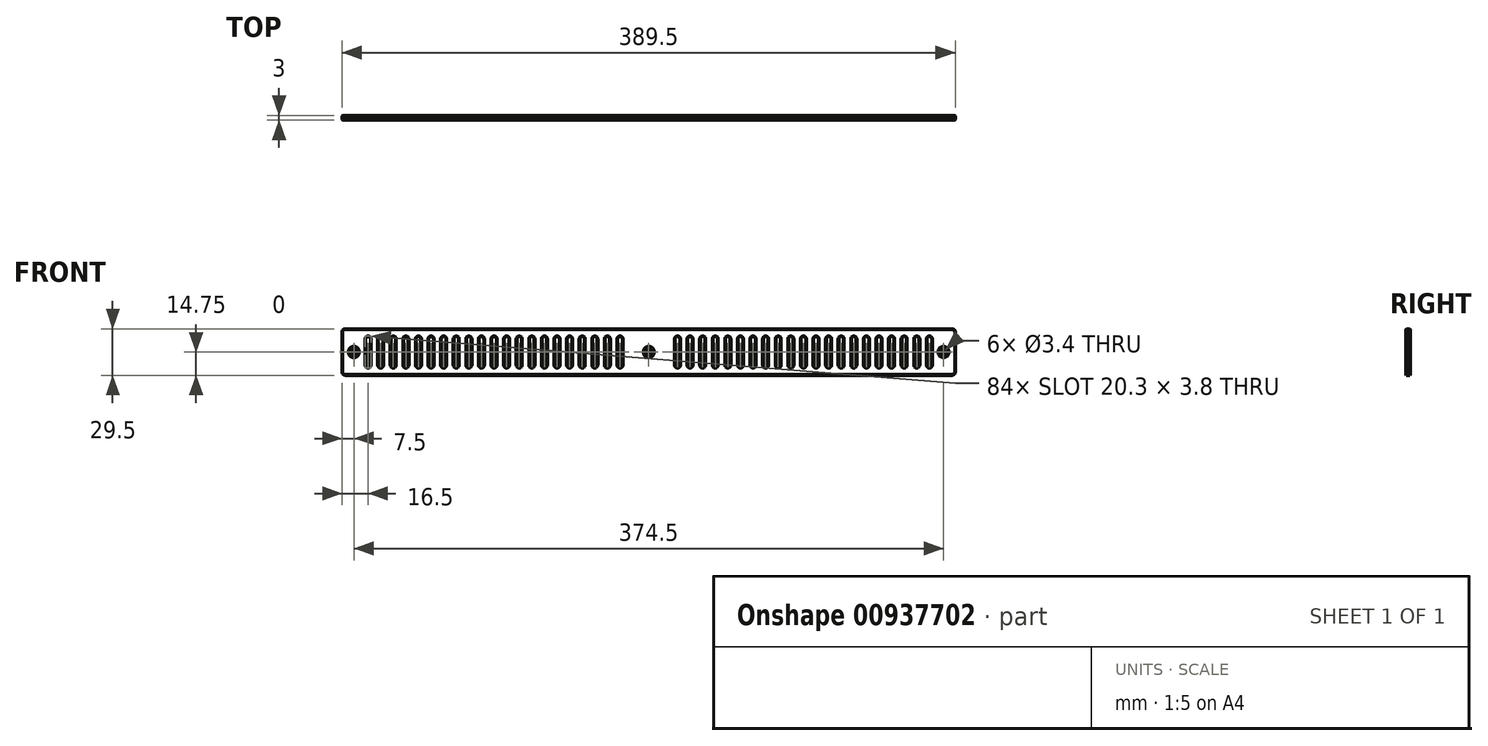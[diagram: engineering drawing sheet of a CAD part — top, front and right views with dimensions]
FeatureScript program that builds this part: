
annotation { "Feature Type Name" : "Feature", "Feature Type Description" : "" }
export const myFeature = defineFeature(function(context is Context, id is Id, definition is map)
    precondition{}
    {
        {
            var Q0;
            Q0=qCreatedBy(makeId("Front.planeOp"),FACE);
            var sketch = newSketch(context, id + "F0", { "sketchPlane" : qUnion([Q0])});
            skLineSegment(sketch, "E0.bottom", {"start": v(-194.75, 14.75) * mm, "end": v(194.75, 14.75) * mm});
            skLineSegment(sketch, "E0.top", {"start": v(-194.75, -14.75) * mm, "end": v(194.75, -14.75) * mm});
            skLineSegment(sketch, "E0.left", {"start": v(-194.75, 14.75) * mm, "end": v(-194.75, -14.75) * mm});
            skLineSegment(sketch, "E0.right", {"start": v(194.75, 14.75) * mm, "end": v(194.75, -14.75) * mm});
            skLineSegment(sketch, "E1.bottom", {"start": v(-178.25, 9.75) * mm, "end": v(-178.25, 9.75) * mm});
            skLineSegment(sketch, "E1.top", {"start": v(-178.25, -9.75) * mm, "end": v(-178.25, -9.75) * mm});
            skLineSegment(sketch, "E1.left", {"start": v(-179.75, 8.25) * mm, "end": v(-179.75, -8.25) * mm});
            skLineSegment(sketch, "E1.right", {"start": v(-176.75, 8.25) * mm, "end": v(-176.75, -8.25) * mm});
            skPoint(sketch, "E2.visualSharp", {"position": v(-179.75, 9.75) * mm});
            skArc(sketch, "E2.filletArc", {"start": v(-178.25, 9.75) * mm, "mid": v(-179.31, 9.31) * mm, "end": v(-179.75, 8.25) * mm});
            skPoint(sketch, "E3.visualSharp", {"position": v(-176.75, 9.75) * mm});
            skArc(sketch, "E3.filletArc", {"start": v(-176.75, 8.25) * mm, "mid": v(-177.19, 9.31) * mm, "end": v(-178.25, 9.75) * mm});
            skPoint(sketch, "E4.visualSharp", {"position": v(-179.75, -9.75) * mm});
            skArc(sketch, "E4.filletArc", {"start": v(-179.75, -8.25) * mm, "mid": v(-179.31, -9.31) * mm, "end": v(-178.25, -9.75) * mm});
            skPoint(sketch, "E5.visualSharp", {"position": v(-176.75, -9.75) * mm});
            skArc(sketch, "E5.filletArc", {"start": v(-178.25, -9.75) * mm, "mid": v(-177.19, -9.31) * mm, "end": v(-176.75, -8.25) * mm});
            skLineSegment(sketch, "E6.1.0.0", {"start": v(-171.75, 8.25) * mm, "end": v(-171.75, -8.25) * mm});
            skPoint(sketch, "E6.1.0.1", {"position": v(-168.75, -9.75) * mm});
            skPoint(sketch, "E6.1.0.2", {"position": v(-171.75, 9.75) * mm});
            skPoint(sketch, "E6.1.0.3", {"position": v(-171.75, -9.75) * mm});
            skLineSegment(sketch, "E6.1.0.4", {"start": v(-168.75, 8.25) * mm, "end": v(-168.75, -8.25) * mm});
            skPoint(sketch, "E6.1.0.5", {"position": v(-168.75, 9.75) * mm});
            skArc(sketch, "E6.1.0.6", {"start": v(-170.25, -9.75) * mm, "mid": v(-169.19, -9.31) * mm, "end": v(-168.75, -8.25) * mm});
            skArc(sketch, "E6.1.0.7", {"start": v(-170.25, 9.75) * mm, "mid": v(-171.31, 9.31) * mm, "end": v(-171.75, 8.25) * mm});
            skArc(sketch, "E6.1.0.8", {"start": v(-168.75, 8.25) * mm, "mid": v(-169.19, 9.31) * mm, "end": v(-170.25, 9.75) * mm});
            skArc(sketch, "E6.1.0.9", {"start": v(-171.75, -8.25) * mm, "mid": v(-171.31, -9.31) * mm, "end": v(-170.25, -9.75) * mm});
            skLineSegment(sketch, "E6.2.0.0", {"start": v(-163.75, 8.25) * mm, "end": v(-163.75, -8.25) * mm});
            skPoint(sketch, "E6.2.0.1", {"position": v(-160.75, -9.75) * mm});
            skPoint(sketch, "E6.2.0.2", {"position": v(-163.75, 9.75) * mm});
            skPoint(sketch, "E6.2.0.3", {"position": v(-163.75, -9.75) * mm});
            skLineSegment(sketch, "E6.2.0.4", {"start": v(-160.75, 8.25) * mm, "end": v(-160.75, -8.25) * mm});
            skPoint(sketch, "E6.2.0.5", {"position": v(-160.75, 9.75) * mm});
            skArc(sketch, "E6.2.0.6", {"start": v(-162.25, -9.75) * mm, "mid": v(-161.19, -9.31) * mm, "end": v(-160.75, -8.25) * mm});
            skArc(sketch, "E6.2.0.7", {"start": v(-162.25, 9.75) * mm, "mid": v(-163.31, 9.31) * mm, "end": v(-163.75, 8.25) * mm});
            skArc(sketch, "E6.2.0.8", {"start": v(-160.75, 8.25) * mm, "mid": v(-161.19, 9.31) * mm, "end": v(-162.25, 9.75) * mm});
            skArc(sketch, "E6.2.0.9", {"start": v(-163.75, -8.25) * mm, "mid": v(-163.31, -9.31) * mm, "end": v(-162.25, -9.75) * mm});
            skLineSegment(sketch, "E6.3.0.0", {"start": v(-155.75, 8.25) * mm, "end": v(-155.75, -8.25) * mm});
            skPoint(sketch, "E6.3.0.1", {"position": v(-152.75, -9.75) * mm});
            skPoint(sketch, "E6.3.0.2", {"position": v(-155.75, 9.75) * mm});
            skPoint(sketch, "E6.3.0.3", {"position": v(-155.75, -9.75) * mm});
            skLineSegment(sketch, "E6.3.0.4", {"start": v(-152.75, 8.25) * mm, "end": v(-152.75, -8.25) * mm});
            skPoint(sketch, "E6.3.0.5", {"position": v(-152.75, 9.75) * mm});
            skArc(sketch, "E6.3.0.6", {"start": v(-154.25, -9.75) * mm, "mid": v(-153.19, -9.31) * mm, "end": v(-152.75, -8.25) * mm});
            skArc(sketch, "E6.3.0.7", {"start": v(-154.25, 9.75) * mm, "mid": v(-155.31, 9.31) * mm, "end": v(-155.75, 8.25) * mm});
            skArc(sketch, "E6.3.0.8", {"start": v(-152.75, 8.25) * mm, "mid": v(-153.19, 9.31) * mm, "end": v(-154.25, 9.75) * mm});
            skArc(sketch, "E6.3.0.9", {"start": v(-155.75, -8.25) * mm, "mid": v(-155.31, -9.31) * mm, "end": v(-154.25, -9.75) * mm});
            skLineSegment(sketch, "E6.4.0.0", {"start": v(-147.75, 8.25) * mm, "end": v(-147.75, -8.25) * mm});
            skPoint(sketch, "E6.4.0.1", {"position": v(-144.75, -9.75) * mm});
            skPoint(sketch, "E6.4.0.2", {"position": v(-147.75, 9.75) * mm});
            skPoint(sketch, "E6.4.0.3", {"position": v(-147.75, -9.75) * mm});
            skLineSegment(sketch, "E6.4.0.4", {"start": v(-144.75, 8.25) * mm, "end": v(-144.75, -8.25) * mm});
            skPoint(sketch, "E6.4.0.5", {"position": v(-144.75, 9.75) * mm});
            skArc(sketch, "E6.4.0.6", {"start": v(-146.25, -9.75) * mm, "mid": v(-145.19, -9.31) * mm, "end": v(-144.75, -8.25) * mm});
            skArc(sketch, "E6.4.0.7", {"start": v(-146.25, 9.75) * mm, "mid": v(-147.31, 9.31) * mm, "end": v(-147.75, 8.25) * mm});
            skArc(sketch, "E6.4.0.8", {"start": v(-144.75, 8.25) * mm, "mid": v(-145.19, 9.31) * mm, "end": v(-146.25, 9.75) * mm});
            skArc(sketch, "E6.4.0.9", {"start": v(-147.75, -8.25) * mm, "mid": v(-147.31, -9.31) * mm, "end": v(-146.25, -9.75) * mm});
            skLineSegment(sketch, "E6.5.0.0", {"start": v(-139.75, 8.25) * mm, "end": v(-139.75, -8.25) * mm});
            skPoint(sketch, "E6.5.0.1", {"position": v(-136.75, -9.75) * mm});
            skPoint(sketch, "E6.5.0.2", {"position": v(-139.75, 9.75) * mm});
            skPoint(sketch, "E6.5.0.3", {"position": v(-139.75, -9.75) * mm});
            skLineSegment(sketch, "E6.5.0.4", {"start": v(-136.75, 8.25) * mm, "end": v(-136.75, -8.25) * mm});
            skPoint(sketch, "E6.5.0.5", {"position": v(-136.75, 9.75) * mm});
            skArc(sketch, "E6.5.0.6", {"start": v(-138.25, -9.75) * mm, "mid": v(-137.19, -9.31) * mm, "end": v(-136.75, -8.25) * mm});
            skArc(sketch, "E6.5.0.7", {"start": v(-138.25, 9.75) * mm, "mid": v(-139.31, 9.31) * mm, "end": v(-139.75, 8.25) * mm});
            skArc(sketch, "E6.5.0.8", {"start": v(-136.75, 8.25) * mm, "mid": v(-137.19, 9.31) * mm, "end": v(-138.25, 9.75) * mm});
            skArc(sketch, "E6.5.0.9", {"start": v(-139.75, -8.25) * mm, "mid": v(-139.31, -9.31) * mm, "end": v(-138.25, -9.75) * mm});
            skLineSegment(sketch, "E6.6.0.0", {"start": v(-131.75, 8.25) * mm, "end": v(-131.75, -8.25) * mm});
            skPoint(sketch, "E6.6.0.1", {"position": v(-128.75, -9.75) * mm});
            skPoint(sketch, "E6.6.0.2", {"position": v(-131.75, 9.75) * mm});
            skPoint(sketch, "E6.6.0.3", {"position": v(-131.75, -9.75) * mm});
            skLineSegment(sketch, "E6.6.0.4", {"start": v(-128.75, 8.25) * mm, "end": v(-128.75, -8.25) * mm});
            skPoint(sketch, "E6.6.0.5", {"position": v(-128.75, 9.75) * mm});
            skArc(sketch, "E6.6.0.6", {"start": v(-130.25, -9.75) * mm, "mid": v(-129.19, -9.31) * mm, "end": v(-128.75, -8.25) * mm});
            skArc(sketch, "E6.6.0.7", {"start": v(-130.25, 9.75) * mm, "mid": v(-131.31, 9.31) * mm, "end": v(-131.75, 8.25) * mm});
            skArc(sketch, "E6.6.0.8", {"start": v(-128.75, 8.25) * mm, "mid": v(-129.19, 9.31) * mm, "end": v(-130.25, 9.75) * mm});
            skArc(sketch, "E6.6.0.9", {"start": v(-131.75, -8.25) * mm, "mid": v(-131.31, -9.31) * mm, "end": v(-130.25, -9.75) * mm});
            skLineSegment(sketch, "E6.7.0.0", {"start": v(-123.75, 8.25) * mm, "end": v(-123.75, -8.25) * mm});
            skPoint(sketch, "E6.7.0.1", {"position": v(-120.75, -9.75) * mm});
            skPoint(sketch, "E6.7.0.2", {"position": v(-123.75, 9.75) * mm});
            skPoint(sketch, "E6.7.0.3", {"position": v(-123.75, -9.75) * mm});
            skLineSegment(sketch, "E6.7.0.4", {"start": v(-120.75, 8.25) * mm, "end": v(-120.75, -8.25) * mm});
            skPoint(sketch, "E6.7.0.5", {"position": v(-120.75, 9.75) * mm});
            skArc(sketch, "E6.7.0.6", {"start": v(-122.25, -9.75) * mm, "mid": v(-121.19, -9.31) * mm, "end": v(-120.75, -8.25) * mm});
            skArc(sketch, "E6.7.0.7", {"start": v(-122.25, 9.75) * mm, "mid": v(-123.31, 9.31) * mm, "end": v(-123.75, 8.25) * mm});
            skArc(sketch, "E6.7.0.8", {"start": v(-120.75, 8.25) * mm, "mid": v(-121.19, 9.31) * mm, "end": v(-122.25, 9.75) * mm});
            skArc(sketch, "E6.7.0.9", {"start": v(-123.75, -8.25) * mm, "mid": v(-123.31, -9.31) * mm, "end": v(-122.25, -9.75) * mm});
            skLineSegment(sketch, "E6.8.0.0", {"start": v(-115.75, 8.25) * mm, "end": v(-115.75, -8.25) * mm});
            skPoint(sketch, "E6.8.0.1", {"position": v(-112.75, -9.75) * mm});
            skPoint(sketch, "E6.8.0.2", {"position": v(-115.75, 9.75) * mm});
            skPoint(sketch, "E6.8.0.3", {"position": v(-115.75, -9.75) * mm});
            skLineSegment(sketch, "E6.8.0.4", {"start": v(-112.75, 8.25) * mm, "end": v(-112.75, -8.25) * mm});
            skPoint(sketch, "E6.8.0.5", {"position": v(-112.75, 9.75) * mm});
            skArc(sketch, "E6.8.0.6", {"start": v(-114.25, -9.75) * mm, "mid": v(-113.19, -9.31) * mm, "end": v(-112.75, -8.25) * mm});
            skArc(sketch, "E6.8.0.7", {"start": v(-114.25, 9.75) * mm, "mid": v(-115.31, 9.31) * mm, "end": v(-115.75, 8.25) * mm});
            skArc(sketch, "E6.8.0.8", {"start": v(-112.75, 8.25) * mm, "mid": v(-113.19, 9.31) * mm, "end": v(-114.25, 9.75) * mm});
            skArc(sketch, "E6.8.0.9", {"start": v(-115.75, -8.25) * mm, "mid": v(-115.31, -9.31) * mm, "end": v(-114.25, -9.75) * mm});
            skLineSegment(sketch, "E6.9.0.0", {"start": v(-107.75, 8.25) * mm, "end": v(-107.75, -8.25) * mm});
            skPoint(sketch, "E6.9.0.1", {"position": v(-104.75, -9.75) * mm});
            skPoint(sketch, "E6.9.0.2", {"position": v(-107.75, 9.75) * mm});
            skPoint(sketch, "E6.9.0.3", {"position": v(-107.75, -9.75) * mm});
            skLineSegment(sketch, "E6.9.0.4", {"start": v(-104.75, 8.25) * mm, "end": v(-104.75, -8.25) * mm});
            skPoint(sketch, "E6.9.0.5", {"position": v(-104.75, 9.75) * mm});
            skArc(sketch, "E6.9.0.6", {"start": v(-106.25, -9.75) * mm, "mid": v(-105.19, -9.31) * mm, "end": v(-104.75, -8.25) * mm});
            skArc(sketch, "E6.9.0.7", {"start": v(-106.25, 9.75) * mm, "mid": v(-107.31, 9.31) * mm, "end": v(-107.75, 8.25) * mm});
            skArc(sketch, "E6.9.0.8", {"start": v(-104.75, 8.25) * mm, "mid": v(-105.19, 9.31) * mm, "end": v(-106.25, 9.75) * mm});
            skArc(sketch, "E6.9.0.9", {"start": v(-107.75, -8.25) * mm, "mid": v(-107.31, -9.31) * mm, "end": v(-106.25, -9.75) * mm});
            skLineSegment(sketch, "E6.10.0.0", {"start": v(-99.75, 8.25) * mm, "end": v(-99.75, -8.25) * mm});
            skPoint(sketch, "E6.10.0.1", {"position": v(-96.75, -9.75) * mm});
            skPoint(sketch, "E6.10.0.2", {"position": v(-99.75, 9.75) * mm});
            skPoint(sketch, "E6.10.0.3", {"position": v(-99.75, -9.75) * mm});
            skLineSegment(sketch, "E6.10.0.4", {"start": v(-96.75, 8.25) * mm, "end": v(-96.75, -8.25) * mm});
            skPoint(sketch, "E6.10.0.5", {"position": v(-96.75, 9.75) * mm});
            skArc(sketch, "E6.10.0.6", {"start": v(-98.25, -9.75) * mm, "mid": v(-97.19, -9.31) * mm, "end": v(-96.75, -8.25) * mm});
            skArc(sketch, "E6.10.0.7", {"start": v(-98.25, 9.75) * mm, "mid": v(-99.31, 9.31) * mm, "end": v(-99.75, 8.25) * mm});
            skArc(sketch, "E6.10.0.8", {"start": v(-96.75, 8.25) * mm, "mid": v(-97.19, 9.31) * mm, "end": v(-98.25, 9.75) * mm});
            skArc(sketch, "E6.10.0.9", {"start": v(-99.75, -8.25) * mm, "mid": v(-99.31, -9.31) * mm, "end": v(-98.25, -9.75) * mm});
            skLineSegment(sketch, "E6.11.0.0", {"start": v(-91.75, 8.25) * mm, "end": v(-91.75, -8.25) * mm});
            skPoint(sketch, "E6.11.0.1", {"position": v(-88.75, -9.75) * mm});
            skPoint(sketch, "E6.11.0.2", {"position": v(-91.75, 9.75) * mm});
            skPoint(sketch, "E6.11.0.3", {"position": v(-91.75, -9.75) * mm});
            skLineSegment(sketch, "E6.11.0.4", {"start": v(-88.75, 8.25) * mm, "end": v(-88.75, -8.25) * mm});
            skPoint(sketch, "E6.11.0.5", {"position": v(-88.75, 9.75) * mm});
            skArc(sketch, "E6.11.0.6", {"start": v(-90.25, -9.75) * mm, "mid": v(-89.19, -9.31) * mm, "end": v(-88.75, -8.25) * mm});
            skArc(sketch, "E6.11.0.7", {"start": v(-90.25, 9.75) * mm, "mid": v(-91.31, 9.31) * mm, "end": v(-91.75, 8.25) * mm});
            skArc(sketch, "E6.11.0.8", {"start": v(-88.75, 8.25) * mm, "mid": v(-89.19, 9.31) * mm, "end": v(-90.25, 9.75) * mm});
            skArc(sketch, "E6.11.0.9", {"start": v(-91.75, -8.25) * mm, "mid": v(-91.31, -9.31) * mm, "end": v(-90.25, -9.75) * mm});
            skLineSegment(sketch, "E6.12.0.0", {"start": v(-83.75, 8.25) * mm, "end": v(-83.75, -8.25) * mm});
            skPoint(sketch, "E6.12.0.1", {"position": v(-80.75, -9.75) * mm});
            skPoint(sketch, "E6.12.0.2", {"position": v(-83.75, 9.75) * mm});
            skPoint(sketch, "E6.12.0.3", {"position": v(-83.75, -9.75) * mm});
            skLineSegment(sketch, "E6.12.0.4", {"start": v(-80.75, 8.25) * mm, "end": v(-80.75, -8.25) * mm});
            skPoint(sketch, "E6.12.0.5", {"position": v(-80.75, 9.75) * mm});
            skArc(sketch, "E6.12.0.6", {"start": v(-82.25, -9.75) * mm, "mid": v(-81.19, -9.31) * mm, "end": v(-80.75, -8.25) * mm});
            skArc(sketch, "E6.12.0.7", {"start": v(-82.25, 9.75) * mm, "mid": v(-83.31, 9.31) * mm, "end": v(-83.75, 8.25) * mm});
            skArc(sketch, "E6.12.0.8", {"start": v(-80.75, 8.25) * mm, "mid": v(-81.19, 9.31) * mm, "end": v(-82.25, 9.75) * mm});
            skArc(sketch, "E6.12.0.9", {"start": v(-83.75, -8.25) * mm, "mid": v(-83.31, -9.31) * mm, "end": v(-82.25, -9.75) * mm});
            skLineSegment(sketch, "E6.13.0.0", {"start": v(-75.75, 8.25) * mm, "end": v(-75.75, -8.25) * mm});
            skPoint(sketch, "E6.13.0.1", {"position": v(-72.75, -9.75) * mm});
            skPoint(sketch, "E6.13.0.2", {"position": v(-75.75, 9.75) * mm});
            skPoint(sketch, "E6.13.0.3", {"position": v(-75.75, -9.75) * mm});
            skLineSegment(sketch, "E6.13.0.4", {"start": v(-72.75, 8.25) * mm, "end": v(-72.75, -8.25) * mm});
            skPoint(sketch, "E6.13.0.5", {"position": v(-72.75, 9.75) * mm});
            skArc(sketch, "E6.13.0.6", {"start": v(-74.25, -9.75) * mm, "mid": v(-73.19, -9.31) * mm, "end": v(-72.75, -8.25) * mm});
            skArc(sketch, "E6.13.0.7", {"start": v(-74.25, 9.75) * mm, "mid": v(-75.31, 9.31) * mm, "end": v(-75.75, 8.25) * mm});
            skArc(sketch, "E6.13.0.8", {"start": v(-72.75, 8.25) * mm, "mid": v(-73.19, 9.31) * mm, "end": v(-74.25, 9.75) * mm});
            skArc(sketch, "E6.13.0.9", {"start": v(-75.75, -8.25) * mm, "mid": v(-75.31, -9.31) * mm, "end": v(-74.25, -9.75) * mm});
            skLineSegment(sketch, "E6.14.0.0", {"start": v(-67.75, 8.25) * mm, "end": v(-67.75, -8.25) * mm});
            skPoint(sketch, "E6.14.0.1", {"position": v(-64.75, -9.75) * mm});
            skPoint(sketch, "E6.14.0.2", {"position": v(-67.75, 9.75) * mm});
            skPoint(sketch, "E6.14.0.3", {"position": v(-67.75, -9.75) * mm});
            skLineSegment(sketch, "E6.14.0.4", {"start": v(-64.75, 8.25) * mm, "end": v(-64.75, -8.25) * mm});
            skPoint(sketch, "E6.14.0.5", {"position": v(-64.75, 9.75) * mm});
            skArc(sketch, "E6.14.0.6", {"start": v(-66.25, -9.75) * mm, "mid": v(-65.19, -9.31) * mm, "end": v(-64.75, -8.25) * mm});
            skArc(sketch, "E6.14.0.7", {"start": v(-66.25, 9.75) * mm, "mid": v(-67.31, 9.31) * mm, "end": v(-67.75, 8.25) * mm});
            skArc(sketch, "E6.14.0.8", {"start": v(-64.75, 8.25) * mm, "mid": v(-65.19, 9.31) * mm, "end": v(-66.25, 9.75) * mm});
            skArc(sketch, "E6.14.0.9", {"start": v(-67.75, -8.25) * mm, "mid": v(-67.31, -9.31) * mm, "end": v(-66.25, -9.75) * mm});
            skLineSegment(sketch, "E6.15.0.0", {"start": v(-59.75, 8.25) * mm, "end": v(-59.75, -8.25) * mm});
            skPoint(sketch, "E6.15.0.1", {"position": v(-56.75, -9.75) * mm});
            skPoint(sketch, "E6.15.0.2", {"position": v(-59.75, 9.75) * mm});
            skPoint(sketch, "E6.15.0.3", {"position": v(-59.75, -9.75) * mm});
            skLineSegment(sketch, "E6.15.0.4", {"start": v(-56.75, 8.25) * mm, "end": v(-56.75, -8.25) * mm});
            skPoint(sketch, "E6.15.0.5", {"position": v(-56.75, 9.75) * mm});
            skArc(sketch, "E6.15.0.6", {"start": v(-58.25, -9.75) * mm, "mid": v(-57.19, -9.31) * mm, "end": v(-56.75, -8.25) * mm});
            skArc(sketch, "E6.15.0.7", {"start": v(-58.25, 9.75) * mm, "mid": v(-59.31, 9.31) * mm, "end": v(-59.75, 8.25) * mm});
            skArc(sketch, "E6.15.0.8", {"start": v(-56.75, 8.25) * mm, "mid": v(-57.19, 9.31) * mm, "end": v(-58.25, 9.75) * mm});
            skArc(sketch, "E6.15.0.9", {"start": v(-59.75, -8.25) * mm, "mid": v(-59.31, -9.31) * mm, "end": v(-58.25, -9.75) * mm});
            skLineSegment(sketch, "E6.16.0.0", {"start": v(-51.75, 8.25) * mm, "end": v(-51.75, -8.25) * mm});
            skPoint(sketch, "E6.16.0.1", {"position": v(-48.75, -9.75) * mm});
            skPoint(sketch, "E6.16.0.2", {"position": v(-51.75, 9.75) * mm});
            skPoint(sketch, "E6.16.0.3", {"position": v(-51.75, -9.75) * mm});
            skLineSegment(sketch, "E6.16.0.4", {"start": v(-48.75, 8.25) * mm, "end": v(-48.75, -8.25) * mm});
            skPoint(sketch, "E6.16.0.5", {"position": v(-48.75, 9.75) * mm});
            skArc(sketch, "E6.16.0.6", {"start": v(-50.25, -9.75) * mm, "mid": v(-49.19, -9.31) * mm, "end": v(-48.75, -8.25) * mm});
            skArc(sketch, "E6.16.0.7", {"start": v(-50.25, 9.75) * mm, "mid": v(-51.31, 9.31) * mm, "end": v(-51.75, 8.25) * mm});
            skArc(sketch, "E6.16.0.8", {"start": v(-48.75, 8.25) * mm, "mid": v(-49.19, 9.31) * mm, "end": v(-50.25, 9.75) * mm});
            skArc(sketch, "E6.16.0.9", {"start": v(-51.75, -8.25) * mm, "mid": v(-51.31, -9.31) * mm, "end": v(-50.25, -9.75) * mm});
            skLineSegment(sketch, "E6.17.0.0", {"start": v(-43.75, 8.25) * mm, "end": v(-43.75, -8.25) * mm});
            skPoint(sketch, "E6.17.0.1", {"position": v(-40.75, -9.75) * mm});
            skPoint(sketch, "E6.17.0.2", {"position": v(-43.75, 9.75) * mm});
            skPoint(sketch, "E6.17.0.3", {"position": v(-43.75, -9.75) * mm});
            skLineSegment(sketch, "E6.17.0.4", {"start": v(-40.75, 8.25) * mm, "end": v(-40.75, -8.25) * mm});
            skPoint(sketch, "E6.17.0.5", {"position": v(-40.75, 9.75) * mm});
            skArc(sketch, "E6.17.0.6", {"start": v(-42.25, -9.75) * mm, "mid": v(-41.19, -9.31) * mm, "end": v(-40.75, -8.25) * mm});
            skArc(sketch, "E6.17.0.7", {"start": v(-42.25, 9.75) * mm, "mid": v(-43.31, 9.31) * mm, "end": v(-43.75, 8.25) * mm});
            skArc(sketch, "E6.17.0.8", {"start": v(-40.75, 8.25) * mm, "mid": v(-41.19, 9.31) * mm, "end": v(-42.25, 9.75) * mm});
            skArc(sketch, "E6.17.0.9", {"start": v(-43.75, -8.25) * mm, "mid": v(-43.31, -9.31) * mm, "end": v(-42.25, -9.75) * mm});
            skLineSegment(sketch, "E6.18.0.0", {"start": v(-35.75, 8.25) * mm, "end": v(-35.75, -8.25) * mm});
            skPoint(sketch, "E6.18.0.1", {"position": v(-32.75, -9.75) * mm});
            skPoint(sketch, "E6.18.0.2", {"position": v(-35.75, 9.75) * mm});
            skPoint(sketch, "E6.18.0.3", {"position": v(-35.75, -9.75) * mm});
            skLineSegment(sketch, "E6.18.0.4", {"start": v(-32.75, 8.25) * mm, "end": v(-32.75, -8.25) * mm});
            skPoint(sketch, "E6.18.0.5", {"position": v(-32.75, 9.75) * mm});
            skArc(sketch, "E6.18.0.6", {"start": v(-34.25, -9.75) * mm, "mid": v(-33.19, -9.31) * mm, "end": v(-32.75, -8.25) * mm});
            skArc(sketch, "E6.18.0.7", {"start": v(-34.25, 9.75) * mm, "mid": v(-35.31, 9.31) * mm, "end": v(-35.75, 8.25) * mm});
            skArc(sketch, "E6.18.0.8", {"start": v(-32.75, 8.25) * mm, "mid": v(-33.19, 9.31) * mm, "end": v(-34.25, 9.75) * mm});
            skArc(sketch, "E6.18.0.9", {"start": v(-35.75, -8.25) * mm, "mid": v(-35.31, -9.31) * mm, "end": v(-34.25, -9.75) * mm});
            skLineSegment(sketch, "E6.19.0.0", {"start": v(-27.75, 8.25) * mm, "end": v(-27.75, -8.25) * mm});
            skPoint(sketch, "E6.19.0.1", {"position": v(-24.75, -9.75) * mm});
            skPoint(sketch, "E6.19.0.2", {"position": v(-27.75, 9.75) * mm});
            skPoint(sketch, "E6.19.0.3", {"position": v(-27.75, -9.75) * mm});
            skLineSegment(sketch, "E6.19.0.4", {"start": v(-24.75, 8.25) * mm, "end": v(-24.75, -8.25) * mm});
            skPoint(sketch, "E6.19.0.5", {"position": v(-24.75, 9.75) * mm});
            skArc(sketch, "E6.19.0.6", {"start": v(-26.25, -9.75) * mm, "mid": v(-25.19, -9.31) * mm, "end": v(-24.75, -8.25) * mm});
            skArc(sketch, "E6.19.0.7", {"start": v(-26.25, 9.75) * mm, "mid": v(-27.31, 9.31) * mm, "end": v(-27.75, 8.25) * mm});
            skArc(sketch, "E6.19.0.8", {"start": v(-24.75, 8.25) * mm, "mid": v(-25.19, 9.31) * mm, "end": v(-26.25, 9.75) * mm});
            skArc(sketch, "E6.19.0.9", {"start": v(-27.75, -8.25) * mm, "mid": v(-27.31, -9.31) * mm, "end": v(-26.25, -9.75) * mm});
            skLineSegment(sketch, "E6.20.0.0", {"start": v(-19.75, 8.25) * mm, "end": v(-19.75, -8.25) * mm});
            skPoint(sketch, "E6.20.0.1", {"position": v(-16.75, -9.75) * mm});
            skPoint(sketch, "E6.20.0.2", {"position": v(-19.75, 9.75) * mm});
            skPoint(sketch, "E6.20.0.3", {"position": v(-19.75, -9.75) * mm});
            skLineSegment(sketch, "E6.20.0.4", {"start": v(-16.75, 8.25) * mm, "end": v(-16.75, -8.25) * mm});
            skPoint(sketch, "E6.20.0.5", {"position": v(-16.75, 9.75) * mm});
            skArc(sketch, "E6.20.0.6", {"start": v(-18.25, -9.75) * mm, "mid": v(-17.19, -9.31) * mm, "end": v(-16.75, -8.25) * mm});
            skArc(sketch, "E6.20.0.7", {"start": v(-18.25, 9.75) * mm, "mid": v(-19.31, 9.31) * mm, "end": v(-19.75, 8.25) * mm});
            skArc(sketch, "E6.20.0.8", {"start": v(-16.75, 8.25) * mm, "mid": v(-17.19, 9.31) * mm, "end": v(-18.25, 9.75) * mm});
            skArc(sketch, "E6.20.0.9", {"start": v(-19.75, -8.25) * mm, "mid": v(-19.31, -9.31) * mm, "end": v(-18.25, -9.75) * mm});
            skLineSegment(sketch, "E6.direction1", {"start": v(-179.75, -9.75) * mm, "end": v(-171.75, -9.75) * mm, "construction": true});
            skLineSegment(sketch, "E7.bottom", {"start": v(178.25, 9.75) * mm, "end": v(178.25, 9.75) * mm});
            skLineSegment(sketch, "E7.top", {"start": v(178.25, -9.75) * mm, "end": v(178.25, -9.75) * mm});
            skLineSegment(sketch, "E7.left", {"start": v(176.75, 8.25) * mm, "end": v(176.75, -8.25) * mm});
            skLineSegment(sketch, "E7.right", {"start": v(179.75, 8.25) * mm, "end": v(179.75, -8.25) * mm});
            skPoint(sketch, "E8.visualSharp", {"position": v(176.75, 9.75) * mm});
            skArc(sketch, "E8.filletArc", {"start": v(178.25, 9.75) * mm, "mid": v(177.19, 9.31) * mm, "end": v(176.75, 8.25) * mm});
            skPoint(sketch, "E9.visualSharp", {"position": v(179.75, 9.75) * mm});
            skArc(sketch, "E9.filletArc", {"start": v(179.75, 8.25) * mm, "mid": v(179.31, 9.31) * mm, "end": v(178.25, 9.75) * mm});
            skPoint(sketch, "E10.visualSharp", {"position": v(176.75, -9.75) * mm});
            skArc(sketch, "E10.filletArc", {"start": v(176.75, -8.25) * mm, "mid": v(177.19, -9.31) * mm, "end": v(178.25, -9.75) * mm});
            skPoint(sketch, "E11.visualSharp", {"position": v(179.75, -9.75) * mm});
            skArc(sketch, "E11.filletArc", {"start": v(178.25, -9.75) * mm, "mid": v(179.31, -9.31) * mm, "end": v(179.75, -8.25) * mm});
            skLineSegment(sketch, "E12.1.0.0", {"start": v(168.75, 8.25) * mm, "end": v(168.75, -8.25) * mm});
            skPoint(sketch, "E12.1.0.1", {"position": v(168.75, 9.75) * mm});
            skPoint(sketch, "E12.1.0.2", {"position": v(171.75, -9.75) * mm});
            skLineSegment(sketch, "E12.1.0.3", {"start": v(171.75, 8.25) * mm, "end": v(171.75, -8.25) * mm});
            skPoint(sketch, "E12.1.0.4", {"position": v(171.75, 9.75) * mm});
            skPoint(sketch, "E12.1.0.5", {"position": v(168.75, -9.75) * mm});
            skArc(sketch, "E12.1.0.6", {"start": v(170.25, 9.75) * mm, "mid": v(169.19, 9.31) * mm, "end": v(168.75, 8.25) * mm});
            skArc(sketch, "E12.1.0.7", {"start": v(168.75, -8.25) * mm, "mid": v(169.19, -9.31) * mm, "end": v(170.25, -9.75) * mm});
            skArc(sketch, "E12.1.0.8", {"start": v(171.75, 8.25) * mm, "mid": v(171.31, 9.31) * mm, "end": v(170.25, 9.75) * mm});
            skArc(sketch, "E12.1.0.9", {"start": v(170.25, -9.75) * mm, "mid": v(171.31, -9.31) * mm, "end": v(171.75, -8.25) * mm});
            skLineSegment(sketch, "E12.2.0.0", {"start": v(160.75, 8.25) * mm, "end": v(160.75, -8.25) * mm});
            skPoint(sketch, "E12.2.0.1", {"position": v(160.75, 9.75) * mm});
            skPoint(sketch, "E12.2.0.2", {"position": v(163.75, -9.75) * mm});
            skLineSegment(sketch, "E12.2.0.3", {"start": v(163.75, 8.25) * mm, "end": v(163.75, -8.25) * mm});
            skPoint(sketch, "E12.2.0.4", {"position": v(163.75, 9.75) * mm});
            skPoint(sketch, "E12.2.0.5", {"position": v(160.75, -9.75) * mm});
            skArc(sketch, "E12.2.0.6", {"start": v(162.25, 9.75) * mm, "mid": v(161.19, 9.31) * mm, "end": v(160.75, 8.25) * mm});
            skArc(sketch, "E12.2.0.7", {"start": v(160.75, -8.25) * mm, "mid": v(161.19, -9.31) * mm, "end": v(162.25, -9.75) * mm});
            skArc(sketch, "E12.2.0.8", {"start": v(163.75, 8.25) * mm, "mid": v(163.31, 9.31) * mm, "end": v(162.25, 9.75) * mm});
            skArc(sketch, "E12.2.0.9", {"start": v(162.25, -9.75) * mm, "mid": v(163.31, -9.31) * mm, "end": v(163.75, -8.25) * mm});
            skLineSegment(sketch, "E12.3.0.0", {"start": v(152.75, 8.25) * mm, "end": v(152.75, -8.25) * mm});
            skPoint(sketch, "E12.3.0.1", {"position": v(152.75, 9.75) * mm});
            skPoint(sketch, "E12.3.0.2", {"position": v(155.75, -9.75) * mm});
            skLineSegment(sketch, "E12.3.0.3", {"start": v(155.75, 8.25) * mm, "end": v(155.75, -8.25) * mm});
            skPoint(sketch, "E12.3.0.4", {"position": v(155.75, 9.75) * mm});
            skPoint(sketch, "E12.3.0.5", {"position": v(152.75, -9.75) * mm});
            skArc(sketch, "E12.3.0.6", {"start": v(154.25, 9.75) * mm, "mid": v(153.19, 9.31) * mm, "end": v(152.75, 8.25) * mm});
            skArc(sketch, "E12.3.0.7", {"start": v(152.75, -8.25) * mm, "mid": v(153.19, -9.31) * mm, "end": v(154.25, -9.75) * mm});
            skArc(sketch, "E12.3.0.8", {"start": v(155.75, 8.25) * mm, "mid": v(155.31, 9.31) * mm, "end": v(154.25, 9.75) * mm});
            skArc(sketch, "E12.3.0.9", {"start": v(154.25, -9.75) * mm, "mid": v(155.31, -9.31) * mm, "end": v(155.75, -8.25) * mm});
            skLineSegment(sketch, "E12.4.0.0", {"start": v(144.75, 8.25) * mm, "end": v(144.75, -8.25) * mm});
            skPoint(sketch, "E12.4.0.1", {"position": v(144.75, 9.75) * mm});
            skPoint(sketch, "E12.4.0.2", {"position": v(147.75, -9.75) * mm});
            skLineSegment(sketch, "E12.4.0.3", {"start": v(147.75, 8.25) * mm, "end": v(147.75, -8.25) * mm});
            skPoint(sketch, "E12.4.0.4", {"position": v(147.75, 9.75) * mm});
            skPoint(sketch, "E12.4.0.5", {"position": v(144.75, -9.75) * mm});
            skArc(sketch, "E12.4.0.6", {"start": v(146.25, 9.75) * mm, "mid": v(145.19, 9.31) * mm, "end": v(144.75, 8.25) * mm});
            skArc(sketch, "E12.4.0.7", {"start": v(144.75, -8.25) * mm, "mid": v(145.19, -9.31) * mm, "end": v(146.25, -9.75) * mm});
            skArc(sketch, "E12.4.0.8", {"start": v(147.75, 8.25) * mm, "mid": v(147.31, 9.31) * mm, "end": v(146.25, 9.75) * mm});
            skArc(sketch, "E12.4.0.9", {"start": v(146.25, -9.75) * mm, "mid": v(147.31, -9.31) * mm, "end": v(147.75, -8.25) * mm});
            skLineSegment(sketch, "E12.5.0.0", {"start": v(136.75, 8.25) * mm, "end": v(136.75, -8.25) * mm});
            skPoint(sketch, "E12.5.0.1", {"position": v(136.75, 9.75) * mm});
            skPoint(sketch, "E12.5.0.2", {"position": v(139.75, -9.75) * mm});
            skLineSegment(sketch, "E12.5.0.3", {"start": v(139.75, 8.25) * mm, "end": v(139.75, -8.25) * mm});
            skPoint(sketch, "E12.5.0.4", {"position": v(139.75, 9.75) * mm});
            skPoint(sketch, "E12.5.0.5", {"position": v(136.75, -9.75) * mm});
            skArc(sketch, "E12.5.0.6", {"start": v(138.25, 9.75) * mm, "mid": v(137.19, 9.31) * mm, "end": v(136.75, 8.25) * mm});
            skArc(sketch, "E12.5.0.7", {"start": v(136.75, -8.25) * mm, "mid": v(137.19, -9.31) * mm, "end": v(138.25, -9.75) * mm});
            skArc(sketch, "E12.5.0.8", {"start": v(139.75, 8.25) * mm, "mid": v(139.31, 9.31) * mm, "end": v(138.25, 9.75) * mm});
            skArc(sketch, "E12.5.0.9", {"start": v(138.25, -9.75) * mm, "mid": v(139.31, -9.31) * mm, "end": v(139.75, -8.25) * mm});
            skLineSegment(sketch, "E12.6.0.0", {"start": v(128.75, 8.25) * mm, "end": v(128.75, -8.25) * mm});
            skPoint(sketch, "E12.6.0.1", {"position": v(128.75, 9.75) * mm});
            skPoint(sketch, "E12.6.0.2", {"position": v(131.75, -9.75) * mm});
            skLineSegment(sketch, "E12.6.0.3", {"start": v(131.75, 8.25) * mm, "end": v(131.75, -8.25) * mm});
            skPoint(sketch, "E12.6.0.4", {"position": v(131.75, 9.75) * mm});
            skPoint(sketch, "E12.6.0.5", {"position": v(128.75, -9.75) * mm});
            skArc(sketch, "E12.6.0.6", {"start": v(130.25, 9.75) * mm, "mid": v(129.19, 9.31) * mm, "end": v(128.75, 8.25) * mm});
            skArc(sketch, "E12.6.0.7", {"start": v(128.75, -8.25) * mm, "mid": v(129.19, -9.31) * mm, "end": v(130.25, -9.75) * mm});
            skArc(sketch, "E12.6.0.8", {"start": v(131.75, 8.25) * mm, "mid": v(131.31, 9.31) * mm, "end": v(130.25, 9.75) * mm});
            skArc(sketch, "E12.6.0.9", {"start": v(130.25, -9.75) * mm, "mid": v(131.31, -9.31) * mm, "end": v(131.75, -8.25) * mm});
            skLineSegment(sketch, "E12.7.0.0", {"start": v(120.75, 8.25) * mm, "end": v(120.75, -8.25) * mm});
            skPoint(sketch, "E12.7.0.1", {"position": v(120.75, 9.75) * mm});
            skPoint(sketch, "E12.7.0.2", {"position": v(123.75, -9.75) * mm});
            skLineSegment(sketch, "E12.7.0.3", {"start": v(123.75, 8.25) * mm, "end": v(123.75, -8.25) * mm});
            skPoint(sketch, "E12.7.0.4", {"position": v(123.75, 9.75) * mm});
            skPoint(sketch, "E12.7.0.5", {"position": v(120.75, -9.75) * mm});
            skArc(sketch, "E12.7.0.6", {"start": v(122.25, 9.75) * mm, "mid": v(121.19, 9.31) * mm, "end": v(120.75, 8.25) * mm});
            skArc(sketch, "E12.7.0.7", {"start": v(120.75, -8.25) * mm, "mid": v(121.19, -9.31) * mm, "end": v(122.25, -9.75) * mm});
            skArc(sketch, "E12.7.0.8", {"start": v(123.75, 8.25) * mm, "mid": v(123.31, 9.31) * mm, "end": v(122.25, 9.75) * mm});
            skArc(sketch, "E12.7.0.9", {"start": v(122.25, -9.75) * mm, "mid": v(123.31, -9.31) * mm, "end": v(123.75, -8.25) * mm});
            skLineSegment(sketch, "E12.8.0.0", {"start": v(112.75, 8.25) * mm, "end": v(112.75, -8.25) * mm});
            skPoint(sketch, "E12.8.0.1", {"position": v(112.75, 9.75) * mm});
            skPoint(sketch, "E12.8.0.2", {"position": v(115.75, -9.75) * mm});
            skLineSegment(sketch, "E12.8.0.3", {"start": v(115.75, 8.25) * mm, "end": v(115.75, -8.25) * mm});
            skPoint(sketch, "E12.8.0.4", {"position": v(115.75, 9.75) * mm});
            skPoint(sketch, "E12.8.0.5", {"position": v(112.75, -9.75) * mm});
            skArc(sketch, "E12.8.0.6", {"start": v(114.25, 9.75) * mm, "mid": v(113.19, 9.31) * mm, "end": v(112.75, 8.25) * mm});
            skArc(sketch, "E12.8.0.7", {"start": v(112.75, -8.25) * mm, "mid": v(113.19, -9.31) * mm, "end": v(114.25, -9.75) * mm});
            skArc(sketch, "E12.8.0.8", {"start": v(115.75, 8.25) * mm, "mid": v(115.31, 9.31) * mm, "end": v(114.25, 9.75) * mm});
            skArc(sketch, "E12.8.0.9", {"start": v(114.25, -9.75) * mm, "mid": v(115.31, -9.31) * mm, "end": v(115.75, -8.25) * mm});
            skLineSegment(sketch, "E12.9.0.0", {"start": v(104.75, 8.25) * mm, "end": v(104.75, -8.25) * mm});
            skPoint(sketch, "E12.9.0.1", {"position": v(104.75, 9.75) * mm});
            skPoint(sketch, "E12.9.0.2", {"position": v(107.75, -9.75) * mm});
            skLineSegment(sketch, "E12.9.0.3", {"start": v(107.75, 8.25) * mm, "end": v(107.75, -8.25) * mm});
            skPoint(sketch, "E12.9.0.4", {"position": v(107.75, 9.75) * mm});
            skPoint(sketch, "E12.9.0.5", {"position": v(104.75, -9.75) * mm});
            skArc(sketch, "E12.9.0.6", {"start": v(106.25, 9.75) * mm, "mid": v(105.19, 9.31) * mm, "end": v(104.75, 8.25) * mm});
            skArc(sketch, "E12.9.0.7", {"start": v(104.75, -8.25) * mm, "mid": v(105.19, -9.31) * mm, "end": v(106.25, -9.75) * mm});
            skArc(sketch, "E12.9.0.8", {"start": v(107.75, 8.25) * mm, "mid": v(107.31, 9.31) * mm, "end": v(106.25, 9.75) * mm});
            skArc(sketch, "E12.9.0.9", {"start": v(106.25, -9.75) * mm, "mid": v(107.31, -9.31) * mm, "end": v(107.75, -8.25) * mm});
            skLineSegment(sketch, "E12.10.0.0", {"start": v(96.75, 8.25) * mm, "end": v(96.75, -8.25) * mm});
            skPoint(sketch, "E12.10.0.1", {"position": v(96.75, 9.75) * mm});
            skPoint(sketch, "E12.10.0.2", {"position": v(99.75, -9.75) * mm});
            skLineSegment(sketch, "E12.10.0.3", {"start": v(99.75, 8.25) * mm, "end": v(99.75, -8.25) * mm});
            skPoint(sketch, "E12.10.0.4", {"position": v(99.75, 9.75) * mm});
            skPoint(sketch, "E12.10.0.5", {"position": v(96.75, -9.75) * mm});
            skArc(sketch, "E12.10.0.6", {"start": v(98.25, 9.75) * mm, "mid": v(97.19, 9.31) * mm, "end": v(96.75, 8.25) * mm});
            skArc(sketch, "E12.10.0.7", {"start": v(96.75, -8.25) * mm, "mid": v(97.19, -9.31) * mm, "end": v(98.25, -9.75) * mm});
            skArc(sketch, "E12.10.0.8", {"start": v(99.75, 8.25) * mm, "mid": v(99.31, 9.31) * mm, "end": v(98.25, 9.75) * mm});
            skArc(sketch, "E12.10.0.9", {"start": v(98.25, -9.75) * mm, "mid": v(99.31, -9.31) * mm, "end": v(99.75, -8.25) * mm});
            skLineSegment(sketch, "E12.11.0.0", {"start": v(88.75, 8.25) * mm, "end": v(88.75, -8.25) * mm});
            skPoint(sketch, "E12.11.0.1", {"position": v(88.75, 9.75) * mm});
            skPoint(sketch, "E12.11.0.2", {"position": v(91.75, -9.75) * mm});
            skLineSegment(sketch, "E12.11.0.3", {"start": v(91.75, 8.25) * mm, "end": v(91.75, -8.25) * mm});
            skPoint(sketch, "E12.11.0.4", {"position": v(91.75, 9.75) * mm});
            skPoint(sketch, "E12.11.0.5", {"position": v(88.75, -9.75) * mm});
            skArc(sketch, "E12.11.0.6", {"start": v(90.25, 9.75) * mm, "mid": v(89.19, 9.31) * mm, "end": v(88.75, 8.25) * mm});
            skArc(sketch, "E12.11.0.7", {"start": v(88.75, -8.25) * mm, "mid": v(89.19, -9.31) * mm, "end": v(90.25, -9.75) * mm});
            skArc(sketch, "E12.11.0.8", {"start": v(91.75, 8.25) * mm, "mid": v(91.31, 9.31) * mm, "end": v(90.25, 9.75) * mm});
            skArc(sketch, "E12.11.0.9", {"start": v(90.25, -9.75) * mm, "mid": v(91.31, -9.31) * mm, "end": v(91.75, -8.25) * mm});
            skLineSegment(sketch, "E12.12.0.0", {"start": v(80.75, 8.25) * mm, "end": v(80.75, -8.25) * mm});
            skPoint(sketch, "E12.12.0.1", {"position": v(80.75, 9.75) * mm});
            skPoint(sketch, "E12.12.0.2", {"position": v(83.75, -9.75) * mm});
            skLineSegment(sketch, "E12.12.0.3", {"start": v(83.75, 8.25) * mm, "end": v(83.75, -8.25) * mm});
            skPoint(sketch, "E12.12.0.4", {"position": v(83.75, 9.75) * mm});
            skPoint(sketch, "E12.12.0.5", {"position": v(80.75, -9.75) * mm});
            skArc(sketch, "E12.12.0.6", {"start": v(82.25, 9.75) * mm, "mid": v(81.19, 9.31) * mm, "end": v(80.75, 8.25) * mm});
            skArc(sketch, "E12.12.0.7", {"start": v(80.75, -8.25) * mm, "mid": v(81.19, -9.31) * mm, "end": v(82.25, -9.75) * mm});
            skArc(sketch, "E12.12.0.8", {"start": v(83.75, 8.25) * mm, "mid": v(83.31, 9.31) * mm, "end": v(82.25, 9.75) * mm});
            skArc(sketch, "E12.12.0.9", {"start": v(82.25, -9.75) * mm, "mid": v(83.31, -9.31) * mm, "end": v(83.75, -8.25) * mm});
            skLineSegment(sketch, "E12.13.0.0", {"start": v(72.75, 8.25) * mm, "end": v(72.75, -8.25) * mm});
            skPoint(sketch, "E12.13.0.1", {"position": v(72.75, 9.75) * mm});
            skPoint(sketch, "E12.13.0.2", {"position": v(75.75, -9.75) * mm});
            skLineSegment(sketch, "E12.13.0.3", {"start": v(75.75, 8.25) * mm, "end": v(75.75, -8.25) * mm});
            skPoint(sketch, "E12.13.0.4", {"position": v(75.75, 9.75) * mm});
            skPoint(sketch, "E12.13.0.5", {"position": v(72.75, -9.75) * mm});
            skArc(sketch, "E12.13.0.6", {"start": v(74.25, 9.75) * mm, "mid": v(73.19, 9.31) * mm, "end": v(72.75, 8.25) * mm});
            skArc(sketch, "E12.13.0.7", {"start": v(72.75, -8.25) * mm, "mid": v(73.19, -9.31) * mm, "end": v(74.25, -9.75) * mm});
            skArc(sketch, "E12.13.0.8", {"start": v(75.75, 8.25) * mm, "mid": v(75.31, 9.31) * mm, "end": v(74.25, 9.75) * mm});
            skArc(sketch, "E12.13.0.9", {"start": v(74.25, -9.75) * mm, "mid": v(75.31, -9.31) * mm, "end": v(75.75, -8.25) * mm});
            skLineSegment(sketch, "E12.14.0.0", {"start": v(64.75, 8.25) * mm, "end": v(64.75, -8.25) * mm});
            skPoint(sketch, "E12.14.0.1", {"position": v(64.75, 9.75) * mm});
            skPoint(sketch, "E12.14.0.2", {"position": v(67.75, -9.75) * mm});
            skLineSegment(sketch, "E12.14.0.3", {"start": v(67.75, 8.25) * mm, "end": v(67.75, -8.25) * mm});
            skPoint(sketch, "E12.14.0.4", {"position": v(67.75, 9.75) * mm});
            skPoint(sketch, "E12.14.0.5", {"position": v(64.75, -9.75) * mm});
            skArc(sketch, "E12.14.0.6", {"start": v(66.25, 9.75) * mm, "mid": v(65.19, 9.31) * mm, "end": v(64.75, 8.25) * mm});
            skArc(sketch, "E12.14.0.7", {"start": v(64.75, -8.25) * mm, "mid": v(65.19, -9.31) * mm, "end": v(66.25, -9.75) * mm});
            skArc(sketch, "E12.14.0.8", {"start": v(67.75, 8.25) * mm, "mid": v(67.31, 9.31) * mm, "end": v(66.25, 9.75) * mm});
            skArc(sketch, "E12.14.0.9", {"start": v(66.25, -9.75) * mm, "mid": v(67.31, -9.31) * mm, "end": v(67.75, -8.25) * mm});
            skLineSegment(sketch, "E12.15.0.0", {"start": v(56.75, 8.25) * mm, "end": v(56.75, -8.25) * mm});
            skPoint(sketch, "E12.15.0.1", {"position": v(56.75, 9.75) * mm});
            skPoint(sketch, "E12.15.0.2", {"position": v(59.75, -9.75) * mm});
            skLineSegment(sketch, "E12.15.0.3", {"start": v(59.75, 8.25) * mm, "end": v(59.75, -8.25) * mm});
            skPoint(sketch, "E12.15.0.4", {"position": v(59.75, 9.75) * mm});
            skPoint(sketch, "E12.15.0.5", {"position": v(56.75, -9.75) * mm});
            skArc(sketch, "E12.15.0.6", {"start": v(58.25, 9.75) * mm, "mid": v(57.19, 9.31) * mm, "end": v(56.75, 8.25) * mm});
            skArc(sketch, "E12.15.0.7", {"start": v(56.75, -8.25) * mm, "mid": v(57.19, -9.31) * mm, "end": v(58.25, -9.75) * mm});
            skArc(sketch, "E12.15.0.8", {"start": v(59.75, 8.25) * mm, "mid": v(59.31, 9.31) * mm, "end": v(58.25, 9.75) * mm});
            skArc(sketch, "E12.15.0.9", {"start": v(58.25, -9.75) * mm, "mid": v(59.31, -9.31) * mm, "end": v(59.75, -8.25) * mm});
            skLineSegment(sketch, "E12.16.0.0", {"start": v(48.75, 8.25) * mm, "end": v(48.75, -8.25) * mm});
            skPoint(sketch, "E12.16.0.1", {"position": v(48.75, 9.75) * mm});
            skPoint(sketch, "E12.16.0.2", {"position": v(51.75, -9.75) * mm});
            skLineSegment(sketch, "E12.16.0.3", {"start": v(51.75, 8.25) * mm, "end": v(51.75, -8.25) * mm});
            skPoint(sketch, "E12.16.0.4", {"position": v(51.75, 9.75) * mm});
            skPoint(sketch, "E12.16.0.5", {"position": v(48.75, -9.75) * mm});
            skArc(sketch, "E12.16.0.6", {"start": v(50.25, 9.75) * mm, "mid": v(49.19, 9.31) * mm, "end": v(48.75, 8.25) * mm});
            skArc(sketch, "E12.16.0.7", {"start": v(48.75, -8.25) * mm, "mid": v(49.19, -9.31) * mm, "end": v(50.25, -9.75) * mm});
            skArc(sketch, "E12.16.0.8", {"start": v(51.75, 8.25) * mm, "mid": v(51.31, 9.31) * mm, "end": v(50.25, 9.75) * mm});
            skArc(sketch, "E12.16.0.9", {"start": v(50.25, -9.75) * mm, "mid": v(51.31, -9.31) * mm, "end": v(51.75, -8.25) * mm});
            skLineSegment(sketch, "E12.17.0.0", {"start": v(40.75, 8.25) * mm, "end": v(40.75, -8.25) * mm});
            skPoint(sketch, "E12.17.0.1", {"position": v(40.75, 9.75) * mm});
            skPoint(sketch, "E12.17.0.2", {"position": v(43.75, -9.75) * mm});
            skLineSegment(sketch, "E12.17.0.3", {"start": v(43.75, 8.25) * mm, "end": v(43.75, -8.25) * mm});
            skPoint(sketch, "E12.17.0.4", {"position": v(43.75, 9.75) * mm});
            skPoint(sketch, "E12.17.0.5", {"position": v(40.75, -9.75) * mm});
            skArc(sketch, "E12.17.0.6", {"start": v(42.25, 9.75) * mm, "mid": v(41.19, 9.31) * mm, "end": v(40.75, 8.25) * mm});
            skArc(sketch, "E12.17.0.7", {"start": v(40.75, -8.25) * mm, "mid": v(41.19, -9.31) * mm, "end": v(42.25, -9.75) * mm});
            skArc(sketch, "E12.17.0.8", {"start": v(43.75, 8.25) * mm, "mid": v(43.31, 9.31) * mm, "end": v(42.25, 9.75) * mm});
            skArc(sketch, "E12.17.0.9", {"start": v(42.25, -9.75) * mm, "mid": v(43.31, -9.31) * mm, "end": v(43.75, -8.25) * mm});
            skLineSegment(sketch, "E12.18.0.0", {"start": v(32.75, 8.25) * mm, "end": v(32.75, -8.25) * mm});
            skPoint(sketch, "E12.18.0.1", {"position": v(32.75, 9.75) * mm});
            skPoint(sketch, "E12.18.0.2", {"position": v(35.75, -9.75) * mm});
            skLineSegment(sketch, "E12.18.0.3", {"start": v(35.75, 8.25) * mm, "end": v(35.75, -8.25) * mm});
            skPoint(sketch, "E12.18.0.4", {"position": v(35.75, 9.75) * mm});
            skPoint(sketch, "E12.18.0.5", {"position": v(32.75, -9.75) * mm});
            skArc(sketch, "E12.18.0.6", {"start": v(34.25, 9.75) * mm, "mid": v(33.19, 9.31) * mm, "end": v(32.75, 8.25) * mm});
            skArc(sketch, "E12.18.0.7", {"start": v(32.75, -8.25) * mm, "mid": v(33.19, -9.31) * mm, "end": v(34.25, -9.75) * mm});
            skArc(sketch, "E12.18.0.8", {"start": v(35.75, 8.25) * mm, "mid": v(35.31, 9.31) * mm, "end": v(34.25, 9.75) * mm});
            skArc(sketch, "E12.18.0.9", {"start": v(34.25, -9.75) * mm, "mid": v(35.31, -9.31) * mm, "end": v(35.75, -8.25) * mm});
            skLineSegment(sketch, "E12.19.0.0", {"start": v(24.75, 8.25) * mm, "end": v(24.75, -8.25) * mm});
            skPoint(sketch, "E12.19.0.1", {"position": v(24.75, 9.75) * mm});
            skPoint(sketch, "E12.19.0.2", {"position": v(27.75, -9.75) * mm});
            skLineSegment(sketch, "E12.19.0.3", {"start": v(27.75, 8.25) * mm, "end": v(27.75, -8.25) * mm});
            skPoint(sketch, "E12.19.0.4", {"position": v(27.75, 9.75) * mm});
            skPoint(sketch, "E12.19.0.5", {"position": v(24.75, -9.75) * mm});
            skArc(sketch, "E12.19.0.6", {"start": v(26.25, 9.75) * mm, "mid": v(25.19, 9.31) * mm, "end": v(24.75, 8.25) * mm});
            skArc(sketch, "E12.19.0.7", {"start": v(24.75, -8.25) * mm, "mid": v(25.19, -9.31) * mm, "end": v(26.25, -9.75) * mm});
            skArc(sketch, "E12.19.0.8", {"start": v(27.75, 8.25) * mm, "mid": v(27.31, 9.31) * mm, "end": v(26.25, 9.75) * mm});
            skArc(sketch, "E12.19.0.9", {"start": v(26.25, -9.75) * mm, "mid": v(27.31, -9.31) * mm, "end": v(27.75, -8.25) * mm});
            skLineSegment(sketch, "E12.20.0.0", {"start": v(16.75, 8.25) * mm, "end": v(16.75, -8.25) * mm});
            skPoint(sketch, "E12.20.0.1", {"position": v(16.75, 9.75) * mm});
            skPoint(sketch, "E12.20.0.2", {"position": v(19.75, -9.75) * mm});
            skLineSegment(sketch, "E12.20.0.3", {"start": v(19.75, 8.25) * mm, "end": v(19.75, -8.25) * mm});
            skPoint(sketch, "E12.20.0.4", {"position": v(19.75, 9.75) * mm});
            skPoint(sketch, "E12.20.0.5", {"position": v(16.75, -9.75) * mm});
            skArc(sketch, "E12.20.0.6", {"start": v(18.25, 9.75) * mm, "mid": v(17.19, 9.31) * mm, "end": v(16.75, 8.25) * mm});
            skArc(sketch, "E12.20.0.7", {"start": v(16.75, -8.25) * mm, "mid": v(17.19, -9.31) * mm, "end": v(18.25, -9.75) * mm});
            skArc(sketch, "E12.20.0.8", {"start": v(19.75, 8.25) * mm, "mid": v(19.31, 9.31) * mm, "end": v(18.25, 9.75) * mm});
            skArc(sketch, "E12.20.0.9", {"start": v(18.25, -9.75) * mm, "mid": v(19.31, -9.31) * mm, "end": v(19.75, -8.25) * mm});
            skLineSegment(sketch, "E12.direction1", {"start": v(176.75, -9.75) * mm, "end": v(168.75, -9.75) * mm, "construction": true});
            skSolve(sketch);
        }
        {
            var Q0;
            Q0=makeQuery(id+"F0.imprint","IMPRINT",FACE,{"disambiguationData":[TD([[makeQuery(id+"F0.imprint","IMPRINT",EDGE,{"derivedFrom":sQuery(id+"F0.wireOp",EDGE,"E0.bottom")}),-1.0]])]});
            extrude(context, id + "F1", {"entities" : qUnion([Q0]), "depth" : 3 * mm, "offsetDistance" : 25 * mm});
        }
        {
            var Q0;
            Q0=makeQuery(id+"F1.opExtrude","CAP_FACE",FACE,{"disambiguationData":[OSD([sQuery(id+"F0.wireOp",EDGE,"E0.bottom"),sQuery(id+"F0.wireOp",EDGE,"E0.top"),sQuery(id+"F0.wireOp",EDGE,"E0.left"),sQuery(id+"F0.wireOp",EDGE,"E0.right"),sQuery(id+"F0.wireOp",EDGE,"E1.left"),sQuery(id+"F0.wireOp",EDGE,"E1.right"),sQuery(id+"F0.wireOp",EDGE,"E2.filletArc"),sQuery(id+"F0.wireOp",EDGE,"E3.filletArc"),sQuery(id+"F0.wireOp",EDGE,"E4.filletArc"),sQuery(id+"F0.wireOp",EDGE,"E5.filletArc"),sQuery(id+"F0.wireOp",EDGE,"E6.1.0.0"),sQuery(id+"F0.wireOp",EDGE,"E6.1.0.4"),sQuery(id+"F0.wireOp",EDGE,"E6.1.0.6"),sQuery(id+"F0.wireOp",EDGE,"E6.1.0.7"),sQuery(id+"F0.wireOp",EDGE,"E6.1.0.8"),sQuery(id+"F0.wireOp",EDGE,"E6.1.0.9"),sQuery(id+"F0.wireOp",EDGE,"E6.2.0.0"),sQuery(id+"F0.wireOp",EDGE,"E6.2.0.4"),sQuery(id+"F0.wireOp",EDGE,"E6.2.0.6"),sQuery(id+"F0.wireOp",EDGE,"E6.2.0.7"),sQuery(id+"F0.wireOp",EDGE,"E6.2.0.8"),sQuery(id+"F0.wireOp",EDGE,"E6.2.0.9"),sQuery(id+"F0.wireOp",EDGE,"E6.3.0.0"),sQuery(id+"F0.wireOp",EDGE,"E6.3.0.4"),sQuery(id+"F0.wireOp",EDGE,"E6.3.0.6"),sQuery(id+"F0.wireOp",EDGE,"E6.3.0.7"),sQuery(id+"F0.wireOp",EDGE,"E6.3.0.8"),sQuery(id+"F0.wireOp",EDGE,"E6.3.0.9"),sQuery(id+"F0.wireOp",EDGE,"E6.4.0.0"),sQuery(id+"F0.wireOp",EDGE,"E6.4.0.4"),sQuery(id+"F0.wireOp",EDGE,"E6.4.0.6"),sQuery(id+"F0.wireOp",EDGE,"E6.4.0.7"),sQuery(id+"F0.wireOp",EDGE,"E6.4.0.8"),sQuery(id+"F0.wireOp",EDGE,"E6.4.0.9"),sQuery(id+"F0.wireOp",EDGE,"E6.5.0.0"),sQuery(id+"F0.wireOp",EDGE,"E6.5.0.4"),sQuery(id+"F0.wireOp",EDGE,"E6.5.0.6"),sQuery(id+"F0.wireOp",EDGE,"E6.5.0.7"),sQuery(id+"F0.wireOp",EDGE,"E6.5.0.8"),sQuery(id+"F0.wireOp",EDGE,"E6.5.0.9"),sQuery(id+"F0.wireOp",EDGE,"E6.6.0.0"),sQuery(id+"F0.wireOp",EDGE,"E6.6.0.4"),sQuery(id+"F0.wireOp",EDGE,"E6.6.0.6"),sQuery(id+"F0.wireOp",EDGE,"E6.6.0.7"),sQuery(id+"F0.wireOp",EDGE,"E6.6.0.8"),sQuery(id+"F0.wireOp",EDGE,"E6.6.0.9"),sQuery(id+"F0.wireOp",EDGE,"E6.7.0.0"),sQuery(id+"F0.wireOp",EDGE,"E6.7.0.4"),sQuery(id+"F0.wireOp",EDGE,"E6.7.0.6"),sQuery(id+"F0.wireOp",EDGE,"E6.7.0.7"),sQuery(id+"F0.wireOp",EDGE,"E6.7.0.8"),sQuery(id+"F0.wireOp",EDGE,"E6.7.0.9"),sQuery(id+"F0.wireOp",EDGE,"E6.8.0.0"),sQuery(id+"F0.wireOp",EDGE,"E6.8.0.4"),sQuery(id+"F0.wireOp",EDGE,"E6.8.0.6"),sQuery(id+"F0.wireOp",EDGE,"E6.8.0.7"),sQuery(id+"F0.wireOp",EDGE,"E6.8.0.8"),sQuery(id+"F0.wireOp",EDGE,"E6.8.0.9"),sQuery(id+"F0.wireOp",EDGE,"E6.9.0.0"),sQuery(id+"F0.wireOp",EDGE,"E6.9.0.4"),sQuery(id+"F0.wireOp",EDGE,"E6.9.0.6"),sQuery(id+"F0.wireOp",EDGE,"E6.9.0.7"),sQuery(id+"F0.wireOp",EDGE,"E6.9.0.8"),sQuery(id+"F0.wireOp",EDGE,"E6.9.0.9"),sQuery(id+"F0.wireOp",EDGE,"E6.10.0.0"),sQuery(id+"F0.wireOp",EDGE,"E6.10.0.4"),sQuery(id+"F0.wireOp",EDGE,"E6.10.0.6"),sQuery(id+"F0.wireOp",EDGE,"E6.10.0.7"),sQuery(id+"F0.wireOp",EDGE,"E6.10.0.8"),sQuery(id+"F0.wireOp",EDGE,"E6.10.0.9"),sQuery(id+"F0.wireOp",EDGE,"E6.11.0.0"),sQuery(id+"F0.wireOp",EDGE,"E6.11.0.4"),sQuery(id+"F0.wireOp",EDGE,"E6.11.0.6"),sQuery(id+"F0.wireOp",EDGE,"E6.11.0.7"),sQuery(id+"F0.wireOp",EDGE,"E6.11.0.8"),sQuery(id+"F0.wireOp",EDGE,"E6.11.0.9"),sQuery(id+"F0.wireOp",EDGE,"E6.12.0.0"),sQuery(id+"F0.wireOp",EDGE,"E6.12.0.4"),sQuery(id+"F0.wireOp",EDGE,"E6.12.0.6"),sQuery(id+"F0.wireOp",EDGE,"E6.12.0.7"),sQuery(id+"F0.wireOp",EDGE,"E6.12.0.8"),sQuery(id+"F0.wireOp",EDGE,"E6.12.0.9"),sQuery(id+"F0.wireOp",EDGE,"E6.13.0.0"),sQuery(id+"F0.wireOp",EDGE,"E6.13.0.4"),sQuery(id+"F0.wireOp",EDGE,"E6.13.0.6"),sQuery(id+"F0.wireOp",EDGE,"E6.13.0.7"),sQuery(id+"F0.wireOp",EDGE,"E6.13.0.8"),sQuery(id+"F0.wireOp",EDGE,"E6.13.0.9"),sQuery(id+"F0.wireOp",EDGE,"E6.14.0.0"),sQuery(id+"F0.wireOp",EDGE,"E6.14.0.4"),sQuery(id+"F0.wireOp",EDGE,"E6.14.0.6"),sQuery(id+"F0.wireOp",EDGE,"E6.14.0.7"),sQuery(id+"F0.wireOp",EDGE,"E6.14.0.8"),sQuery(id+"F0.wireOp",EDGE,"E6.14.0.9"),sQuery(id+"F0.wireOp",EDGE,"E6.15.0.0"),sQuery(id+"F0.wireOp",EDGE,"E6.15.0.4"),sQuery(id+"F0.wireOp",EDGE,"E6.15.0.6"),sQuery(id+"F0.wireOp",EDGE,"E6.15.0.7"),sQuery(id+"F0.wireOp",EDGE,"E6.15.0.8"),sQuery(id+"F0.wireOp",EDGE,"E6.15.0.9"),sQuery(id+"F0.wireOp",EDGE,"E6.16.0.0"),sQuery(id+"F0.wireOp",EDGE,"E6.16.0.4"),sQuery(id+"F0.wireOp",EDGE,"E6.16.0.6"),sQuery(id+"F0.wireOp",EDGE,"E6.16.0.7"),sQuery(id+"F0.wireOp",EDGE,"E6.16.0.8"),sQuery(id+"F0.wireOp",EDGE,"E6.16.0.9"),sQuery(id+"F0.wireOp",EDGE,"E6.17.0.0"),sQuery(id+"F0.wireOp",EDGE,"E6.17.0.4"),sQuery(id+"F0.wireOp",EDGE,"E6.17.0.6"),sQuery(id+"F0.wireOp",EDGE,"E6.17.0.7"),sQuery(id+"F0.wireOp",EDGE,"E6.17.0.8"),sQuery(id+"F0.wireOp",EDGE,"E6.17.0.9"),sQuery(id+"F0.wireOp",EDGE,"E6.18.0.0"),sQuery(id+"F0.wireOp",EDGE,"E6.18.0.4"),sQuery(id+"F0.wireOp",EDGE,"E6.18.0.6"),sQuery(id+"F0.wireOp",EDGE,"E6.18.0.7"),sQuery(id+"F0.wireOp",EDGE,"E6.18.0.8"),sQuery(id+"F0.wireOp",EDGE,"E6.18.0.9"),sQuery(id+"F0.wireOp",EDGE,"E6.19.0.0"),sQuery(id+"F0.wireOp",EDGE,"E6.19.0.4"),sQuery(id+"F0.wireOp",EDGE,"E6.19.0.6"),sQuery(id+"F0.wireOp",EDGE,"E6.19.0.7"),sQuery(id+"F0.wireOp",EDGE,"E6.19.0.8"),sQuery(id+"F0.wireOp",EDGE,"E6.19.0.9"),sQuery(id+"F0.wireOp",EDGE,"E6.20.0.0"),sQuery(id+"F0.wireOp",EDGE,"E6.20.0.4"),sQuery(id+"F0.wireOp",EDGE,"E6.20.0.6"),sQuery(id+"F0.wireOp",EDGE,"E6.20.0.7"),sQuery(id+"F0.wireOp",EDGE,"E6.20.0.8"),sQuery(id+"F0.wireOp",EDGE,"E6.20.0.9"),sQuery(id+"F0.wireOp",EDGE,"E7.left"),sQuery(id+"F0.wireOp",EDGE,"E7.right"),sQuery(id+"F0.wireOp",EDGE,"E8.filletArc"),sQuery(id+"F0.wireOp",EDGE,"E9.filletArc"),sQuery(id+"F0.wireOp",EDGE,"E10.filletArc"),sQuery(id+"F0.wireOp",EDGE,"E11.filletArc"),sQuery(id+"F0.wireOp",EDGE,"E12.1.0.0"),sQuery(id+"F0.wireOp",EDGE,"E12.1.0.3"),sQuery(id+"F0.wireOp",EDGE,"E12.1.0.6"),sQuery(id+"F0.wireOp",EDGE,"E12.1.0.7"),sQuery(id+"F0.wireOp",EDGE,"E12.1.0.8"),sQuery(id+"F0.wireOp",EDGE,"E12.1.0.9"),sQuery(id+"F0.wireOp",EDGE,"E12.2.0.0"),sQuery(id+"F0.wireOp",EDGE,"E12.2.0.3"),sQuery(id+"F0.wireOp",EDGE,"E12.2.0.6"),sQuery(id+"F0.wireOp",EDGE,"E12.2.0.7"),sQuery(id+"F0.wireOp",EDGE,"E12.2.0.8"),sQuery(id+"F0.wireOp",EDGE,"E12.2.0.9"),sQuery(id+"F0.wireOp",EDGE,"E12.3.0.0"),sQuery(id+"F0.wireOp",EDGE,"E12.3.0.3"),sQuery(id+"F0.wireOp",EDGE,"E12.3.0.6"),sQuery(id+"F0.wireOp",EDGE,"E12.3.0.7"),sQuery(id+"F0.wireOp",EDGE,"E12.3.0.8"),sQuery(id+"F0.wireOp",EDGE,"E12.3.0.9"),sQuery(id+"F0.wireOp",EDGE,"E12.4.0.0"),sQuery(id+"F0.wireOp",EDGE,"E12.4.0.3"),sQuery(id+"F0.wireOp",EDGE,"E12.4.0.6"),sQuery(id+"F0.wireOp",EDGE,"E12.4.0.7"),sQuery(id+"F0.wireOp",EDGE,"E12.4.0.8"),sQuery(id+"F0.wireOp",EDGE,"E12.4.0.9"),sQuery(id+"F0.wireOp",EDGE,"E12.5.0.0"),sQuery(id+"F0.wireOp",EDGE,"E12.5.0.3"),sQuery(id+"F0.wireOp",EDGE,"E12.5.0.6"),sQuery(id+"F0.wireOp",EDGE,"E12.5.0.7"),sQuery(id+"F0.wireOp",EDGE,"E12.5.0.8"),sQuery(id+"F0.wireOp",EDGE,"E12.5.0.9"),sQuery(id+"F0.wireOp",EDGE,"E12.6.0.0"),sQuery(id+"F0.wireOp",EDGE,"E12.6.0.3"),sQuery(id+"F0.wireOp",EDGE,"E12.6.0.6"),sQuery(id+"F0.wireOp",EDGE,"E12.6.0.7"),sQuery(id+"F0.wireOp",EDGE,"E12.6.0.8"),sQuery(id+"F0.wireOp",EDGE,"E12.6.0.9"),sQuery(id+"F0.wireOp",EDGE,"E12.7.0.0"),sQuery(id+"F0.wireOp",EDGE,"E12.7.0.3"),sQuery(id+"F0.wireOp",EDGE,"E12.7.0.6"),sQuery(id+"F0.wireOp",EDGE,"E12.7.0.7"),sQuery(id+"F0.wireOp",EDGE,"E12.7.0.8"),sQuery(id+"F0.wireOp",EDGE,"E12.7.0.9"),sQuery(id+"F0.wireOp",EDGE,"E12.8.0.0"),sQuery(id+"F0.wireOp",EDGE,"E12.8.0.3"),sQuery(id+"F0.wireOp",EDGE,"E12.8.0.6"),sQuery(id+"F0.wireOp",EDGE,"E12.8.0.7"),sQuery(id+"F0.wireOp",EDGE,"E12.8.0.8"),sQuery(id+"F0.wireOp",EDGE,"E12.8.0.9"),sQuery(id+"F0.wireOp",EDGE,"E12.9.0.0"),sQuery(id+"F0.wireOp",EDGE,"E12.9.0.3"),sQuery(id+"F0.wireOp",EDGE,"E12.9.0.6"),sQuery(id+"F0.wireOp",EDGE,"E12.9.0.7"),sQuery(id+"F0.wireOp",EDGE,"E12.9.0.8"),sQuery(id+"F0.wireOp",EDGE,"E12.9.0.9"),sQuery(id+"F0.wireOp",EDGE,"E12.10.0.0"),sQuery(id+"F0.wireOp",EDGE,"E12.10.0.3"),sQuery(id+"F0.wireOp",EDGE,"E12.10.0.6"),sQuery(id+"F0.wireOp",EDGE,"E12.10.0.7"),sQuery(id+"F0.wireOp",EDGE,"E12.10.0.8"),sQuery(id+"F0.wireOp",EDGE,"E12.10.0.9"),sQuery(id+"F0.wireOp",EDGE,"E12.11.0.0"),sQuery(id+"F0.wireOp",EDGE,"E12.11.0.3"),sQuery(id+"F0.wireOp",EDGE,"E12.11.0.6"),sQuery(id+"F0.wireOp",EDGE,"E12.11.0.7"),sQuery(id+"F0.wireOp",EDGE,"E12.11.0.8"),sQuery(id+"F0.wireOp",EDGE,"E12.11.0.9"),sQuery(id+"F0.wireOp",EDGE,"E12.12.0.0"),sQuery(id+"F0.wireOp",EDGE,"E12.12.0.3"),sQuery(id+"F0.wireOp",EDGE,"E12.12.0.6"),sQuery(id+"F0.wireOp",EDGE,"E12.12.0.7"),sQuery(id+"F0.wireOp",EDGE,"E12.12.0.8"),sQuery(id+"F0.wireOp",EDGE,"E12.12.0.9"),sQuery(id+"F0.wireOp",EDGE,"E12.13.0.0"),sQuery(id+"F0.wireOp",EDGE,"E12.13.0.3"),sQuery(id+"F0.wireOp",EDGE,"E12.13.0.6"),sQuery(id+"F0.wireOp",EDGE,"E12.13.0.7"),sQuery(id+"F0.wireOp",EDGE,"E12.13.0.8"),sQuery(id+"F0.wireOp",EDGE,"E12.13.0.9"),sQuery(id+"F0.wireOp",EDGE,"E12.14.0.0"),sQuery(id+"F0.wireOp",EDGE,"E12.14.0.3"),sQuery(id+"F0.wireOp",EDGE,"E12.14.0.6"),sQuery(id+"F0.wireOp",EDGE,"E12.14.0.7"),sQuery(id+"F0.wireOp",EDGE,"E12.14.0.8"),sQuery(id+"F0.wireOp",EDGE,"E12.14.0.9"),sQuery(id+"F0.wireOp",EDGE,"E12.15.0.0"),sQuery(id+"F0.wireOp",EDGE,"E12.15.0.3"),sQuery(id+"F0.wireOp",EDGE,"E12.15.0.6"),sQuery(id+"F0.wireOp",EDGE,"E12.15.0.7"),sQuery(id+"F0.wireOp",EDGE,"E12.15.0.8"),sQuery(id+"F0.wireOp",EDGE,"E12.15.0.9"),sQuery(id+"F0.wireOp",EDGE,"E12.16.0.0"),sQuery(id+"F0.wireOp",EDGE,"E12.16.0.3"),sQuery(id+"F0.wireOp",EDGE,"E12.16.0.6"),sQuery(id+"F0.wireOp",EDGE,"E12.16.0.7"),sQuery(id+"F0.wireOp",EDGE,"E12.16.0.8"),sQuery(id+"F0.wireOp",EDGE,"E12.16.0.9"),sQuery(id+"F0.wireOp",EDGE,"E12.17.0.0"),sQuery(id+"F0.wireOp",EDGE,"E12.17.0.3"),sQuery(id+"F0.wireOp",EDGE,"E12.17.0.6"),sQuery(id+"F0.wireOp",EDGE,"E12.17.0.7"),sQuery(id+"F0.wireOp",EDGE,"E12.17.0.8"),sQuery(id+"F0.wireOp",EDGE,"E12.17.0.9"),sQuery(id+"F0.wireOp",EDGE,"E12.18.0.0"),sQuery(id+"F0.wireOp",EDGE,"E12.18.0.3"),sQuery(id+"F0.wireOp",EDGE,"E12.18.0.6"),sQuery(id+"F0.wireOp",EDGE,"E12.18.0.7"),sQuery(id+"F0.wireOp",EDGE,"E12.18.0.8"),sQuery(id+"F0.wireOp",EDGE,"E12.18.0.9"),sQuery(id+"F0.wireOp",EDGE,"E12.19.0.0"),sQuery(id+"F0.wireOp",EDGE,"E12.19.0.3"),sQuery(id+"F0.wireOp",EDGE,"E12.19.0.6"),sQuery(id+"F0.wireOp",EDGE,"E12.19.0.7"),sQuery(id+"F0.wireOp",EDGE,"E12.19.0.8"),sQuery(id+"F0.wireOp",EDGE,"E12.19.0.9"),sQuery(id+"F0.wireOp",EDGE,"E12.20.0.0"),sQuery(id+"F0.wireOp",EDGE,"E12.20.0.3"),sQuery(id+"F0.wireOp",EDGE,"E12.20.0.6"),sQuery(id+"F0.wireOp",EDGE,"E12.20.0.7"),sQuery(id+"F0.wireOp",EDGE,"E12.20.0.8"),sQuery(id+"F0.wireOp",EDGE,"E12.20.0.9")])],"isStart":false});
            var sketch = newSketch(context, id + "F2", { "sketchPlane" : qUnion([Q0])});
            skPoint(sketch, "E13", {"position": v(0, 0) * mm});
            skPoint(sketch, "E14", {"position": v(-187.25, 0) * mm});
            skPoint(sketch, "E15", {"position": v(187.25, 0) * mm});
            skPoint(sketch, "E15.positionSnap0", {"position": v(179.75, 0) * mm});
            skSolve(sketch);
        }
        {
            var Q0;
            Q0=sQuery(id+"F2.wireOp",VERTEX,"E14");
            var Q1;
            Q1=sQuery(id+"F2.wireOp",VERTEX,"E13");
            var Q2;
            Q2=sQuery(id+"F2.wireOp",VERTEX,"E15");
            var Q3;
            Q3=makeQuery(id+"F1.opExtrude","SWEPT_BODY",BODY,{"disambiguationData":[OSD([sQuery(id+"F0.wireOp",EDGE,"E0.bottom"),sQuery(id+"F0.wireOp",EDGE,"E0.top"),sQuery(id+"F0.wireOp",EDGE,"E0.left"),sQuery(id+"F0.wireOp",EDGE,"E0.right"),sQuery(id+"F0.wireOp",EDGE,"E1.left"),sQuery(id+"F0.wireOp",EDGE,"E1.right"),sQuery(id+"F0.wireOp",EDGE,"E2.filletArc"),sQuery(id+"F0.wireOp",EDGE,"E3.filletArc"),sQuery(id+"F0.wireOp",EDGE,"E4.filletArc"),sQuery(id+"F0.wireOp",EDGE,"E5.filletArc"),sQuery(id+"F0.wireOp",EDGE,"E6.1.0.0"),sQuery(id+"F0.wireOp",EDGE,"E6.1.0.4"),sQuery(id+"F0.wireOp",EDGE,"E6.1.0.6"),sQuery(id+"F0.wireOp",EDGE,"E6.1.0.7"),sQuery(id+"F0.wireOp",EDGE,"E6.1.0.8"),sQuery(id+"F0.wireOp",EDGE,"E6.1.0.9"),sQuery(id+"F0.wireOp",EDGE,"E6.2.0.0"),sQuery(id+"F0.wireOp",EDGE,"E6.2.0.4"),sQuery(id+"F0.wireOp",EDGE,"E6.2.0.6"),sQuery(id+"F0.wireOp",EDGE,"E6.2.0.7"),sQuery(id+"F0.wireOp",EDGE,"E6.2.0.8"),sQuery(id+"F0.wireOp",EDGE,"E6.2.0.9"),sQuery(id+"F0.wireOp",EDGE,"E6.3.0.0"),sQuery(id+"F0.wireOp",EDGE,"E6.3.0.4"),sQuery(id+"F0.wireOp",EDGE,"E6.3.0.6"),sQuery(id+"F0.wireOp",EDGE,"E6.3.0.7"),sQuery(id+"F0.wireOp",EDGE,"E6.3.0.8"),sQuery(id+"F0.wireOp",EDGE,"E6.3.0.9"),sQuery(id+"F0.wireOp",EDGE,"E6.4.0.0"),sQuery(id+"F0.wireOp",EDGE,"E6.4.0.4"),sQuery(id+"F0.wireOp",EDGE,"E6.4.0.6"),sQuery(id+"F0.wireOp",EDGE,"E6.4.0.7"),sQuery(id+"F0.wireOp",EDGE,"E6.4.0.8"),sQuery(id+"F0.wireOp",EDGE,"E6.4.0.9"),sQuery(id+"F0.wireOp",EDGE,"E6.5.0.0"),sQuery(id+"F0.wireOp",EDGE,"E6.5.0.4"),sQuery(id+"F0.wireOp",EDGE,"E6.5.0.6"),sQuery(id+"F0.wireOp",EDGE,"E6.5.0.7"),sQuery(id+"F0.wireOp",EDGE,"E6.5.0.8"),sQuery(id+"F0.wireOp",EDGE,"E6.5.0.9"),sQuery(id+"F0.wireOp",EDGE,"E6.6.0.0"),sQuery(id+"F0.wireOp",EDGE,"E6.6.0.4"),sQuery(id+"F0.wireOp",EDGE,"E6.6.0.6"),sQuery(id+"F0.wireOp",EDGE,"E6.6.0.7"),sQuery(id+"F0.wireOp",EDGE,"E6.6.0.8"),sQuery(id+"F0.wireOp",EDGE,"E6.6.0.9"),sQuery(id+"F0.wireOp",EDGE,"E6.7.0.0"),sQuery(id+"F0.wireOp",EDGE,"E6.7.0.4"),sQuery(id+"F0.wireOp",EDGE,"E6.7.0.6"),sQuery(id+"F0.wireOp",EDGE,"E6.7.0.7"),sQuery(id+"F0.wireOp",EDGE,"E6.7.0.8"),sQuery(id+"F0.wireOp",EDGE,"E6.7.0.9"),sQuery(id+"F0.wireOp",EDGE,"E6.8.0.0"),sQuery(id+"F0.wireOp",EDGE,"E6.8.0.4"),sQuery(id+"F0.wireOp",EDGE,"E6.8.0.6"),sQuery(id+"F0.wireOp",EDGE,"E6.8.0.7"),sQuery(id+"F0.wireOp",EDGE,"E6.8.0.8"),sQuery(id+"F0.wireOp",EDGE,"E6.8.0.9"),sQuery(id+"F0.wireOp",EDGE,"E6.9.0.0"),sQuery(id+"F0.wireOp",EDGE,"E6.9.0.4"),sQuery(id+"F0.wireOp",EDGE,"E6.9.0.6"),sQuery(id+"F0.wireOp",EDGE,"E6.9.0.7"),sQuery(id+"F0.wireOp",EDGE,"E6.9.0.8"),sQuery(id+"F0.wireOp",EDGE,"E6.9.0.9"),sQuery(id+"F0.wireOp",EDGE,"E6.10.0.0"),sQuery(id+"F0.wireOp",EDGE,"E6.10.0.4"),sQuery(id+"F0.wireOp",EDGE,"E6.10.0.6"),sQuery(id+"F0.wireOp",EDGE,"E6.10.0.7"),sQuery(id+"F0.wireOp",EDGE,"E6.10.0.8"),sQuery(id+"F0.wireOp",EDGE,"E6.10.0.9"),sQuery(id+"F0.wireOp",EDGE,"E6.11.0.0"),sQuery(id+"F0.wireOp",EDGE,"E6.11.0.4"),sQuery(id+"F0.wireOp",EDGE,"E6.11.0.6"),sQuery(id+"F0.wireOp",EDGE,"E6.11.0.7"),sQuery(id+"F0.wireOp",EDGE,"E6.11.0.8"),sQuery(id+"F0.wireOp",EDGE,"E6.11.0.9"),sQuery(id+"F0.wireOp",EDGE,"E6.12.0.0"),sQuery(id+"F0.wireOp",EDGE,"E6.12.0.4"),sQuery(id+"F0.wireOp",EDGE,"E6.12.0.6"),sQuery(id+"F0.wireOp",EDGE,"E6.12.0.7"),sQuery(id+"F0.wireOp",EDGE,"E6.12.0.8"),sQuery(id+"F0.wireOp",EDGE,"E6.12.0.9"),sQuery(id+"F0.wireOp",EDGE,"E6.13.0.0"),sQuery(id+"F0.wireOp",EDGE,"E6.13.0.4"),sQuery(id+"F0.wireOp",EDGE,"E6.13.0.6"),sQuery(id+"F0.wireOp",EDGE,"E6.13.0.7"),sQuery(id+"F0.wireOp",EDGE,"E6.13.0.8"),sQuery(id+"F0.wireOp",EDGE,"E6.13.0.9"),sQuery(id+"F0.wireOp",EDGE,"E6.14.0.0"),sQuery(id+"F0.wireOp",EDGE,"E6.14.0.4"),sQuery(id+"F0.wireOp",EDGE,"E6.14.0.6"),sQuery(id+"F0.wireOp",EDGE,"E6.14.0.7"),sQuery(id+"F0.wireOp",EDGE,"E6.14.0.8"),sQuery(id+"F0.wireOp",EDGE,"E6.14.0.9"),sQuery(id+"F0.wireOp",EDGE,"E6.15.0.0"),sQuery(id+"F0.wireOp",EDGE,"E6.15.0.4"),sQuery(id+"F0.wireOp",EDGE,"E6.15.0.6"),sQuery(id+"F0.wireOp",EDGE,"E6.15.0.7"),sQuery(id+"F0.wireOp",EDGE,"E6.15.0.8"),sQuery(id+"F0.wireOp",EDGE,"E6.15.0.9"),sQuery(id+"F0.wireOp",EDGE,"E6.16.0.0"),sQuery(id+"F0.wireOp",EDGE,"E6.16.0.4"),sQuery(id+"F0.wireOp",EDGE,"E6.16.0.6"),sQuery(id+"F0.wireOp",EDGE,"E6.16.0.7"),sQuery(id+"F0.wireOp",EDGE,"E6.16.0.8"),sQuery(id+"F0.wireOp",EDGE,"E6.16.0.9"),sQuery(id+"F0.wireOp",EDGE,"E6.17.0.0"),sQuery(id+"F0.wireOp",EDGE,"E6.17.0.4"),sQuery(id+"F0.wireOp",EDGE,"E6.17.0.6"),sQuery(id+"F0.wireOp",EDGE,"E6.17.0.7"),sQuery(id+"F0.wireOp",EDGE,"E6.17.0.8"),sQuery(id+"F0.wireOp",EDGE,"E6.17.0.9"),sQuery(id+"F0.wireOp",EDGE,"E6.18.0.0"),sQuery(id+"F0.wireOp",EDGE,"E6.18.0.4"),sQuery(id+"F0.wireOp",EDGE,"E6.18.0.6"),sQuery(id+"F0.wireOp",EDGE,"E6.18.0.7"),sQuery(id+"F0.wireOp",EDGE,"E6.18.0.8"),sQuery(id+"F0.wireOp",EDGE,"E6.18.0.9"),sQuery(id+"F0.wireOp",EDGE,"E6.19.0.0"),sQuery(id+"F0.wireOp",EDGE,"E6.19.0.4"),sQuery(id+"F0.wireOp",EDGE,"E6.19.0.6"),sQuery(id+"F0.wireOp",EDGE,"E6.19.0.7"),sQuery(id+"F0.wireOp",EDGE,"E6.19.0.8"),sQuery(id+"F0.wireOp",EDGE,"E6.19.0.9"),sQuery(id+"F0.wireOp",EDGE,"E6.20.0.0"),sQuery(id+"F0.wireOp",EDGE,"E6.20.0.4"),sQuery(id+"F0.wireOp",EDGE,"E6.20.0.6"),sQuery(id+"F0.wireOp",EDGE,"E6.20.0.7"),sQuery(id+"F0.wireOp",EDGE,"E6.20.0.8"),sQuery(id+"F0.wireOp",EDGE,"E6.20.0.9"),sQuery(id+"F0.wireOp",EDGE,"E7.left"),sQuery(id+"F0.wireOp",EDGE,"E7.right"),sQuery(id+"F0.wireOp",EDGE,"E8.filletArc"),sQuery(id+"F0.wireOp",EDGE,"E9.filletArc"),sQuery(id+"F0.wireOp",EDGE,"E10.filletArc"),sQuery(id+"F0.wireOp",EDGE,"E11.filletArc"),sQuery(id+"F0.wireOp",EDGE,"E12.1.0.0"),sQuery(id+"F0.wireOp",EDGE,"E12.1.0.3"),sQuery(id+"F0.wireOp",EDGE,"E12.1.0.6"),sQuery(id+"F0.wireOp",EDGE,"E12.1.0.7"),sQuery(id+"F0.wireOp",EDGE,"E12.1.0.8"),sQuery(id+"F0.wireOp",EDGE,"E12.1.0.9"),sQuery(id+"F0.wireOp",EDGE,"E12.2.0.0"),sQuery(id+"F0.wireOp",EDGE,"E12.2.0.3"),sQuery(id+"F0.wireOp",EDGE,"E12.2.0.6"),sQuery(id+"F0.wireOp",EDGE,"E12.2.0.7"),sQuery(id+"F0.wireOp",EDGE,"E12.2.0.8"),sQuery(id+"F0.wireOp",EDGE,"E12.2.0.9"),sQuery(id+"F0.wireOp",EDGE,"E12.3.0.0"),sQuery(id+"F0.wireOp",EDGE,"E12.3.0.3"),sQuery(id+"F0.wireOp",EDGE,"E12.3.0.6"),sQuery(id+"F0.wireOp",EDGE,"E12.3.0.7"),sQuery(id+"F0.wireOp",EDGE,"E12.3.0.8"),sQuery(id+"F0.wireOp",EDGE,"E12.3.0.9"),sQuery(id+"F0.wireOp",EDGE,"E12.4.0.0"),sQuery(id+"F0.wireOp",EDGE,"E12.4.0.3"),sQuery(id+"F0.wireOp",EDGE,"E12.4.0.6"),sQuery(id+"F0.wireOp",EDGE,"E12.4.0.7"),sQuery(id+"F0.wireOp",EDGE,"E12.4.0.8"),sQuery(id+"F0.wireOp",EDGE,"E12.4.0.9"),sQuery(id+"F0.wireOp",EDGE,"E12.5.0.0"),sQuery(id+"F0.wireOp",EDGE,"E12.5.0.3"),sQuery(id+"F0.wireOp",EDGE,"E12.5.0.6"),sQuery(id+"F0.wireOp",EDGE,"E12.5.0.7"),sQuery(id+"F0.wireOp",EDGE,"E12.5.0.8"),sQuery(id+"F0.wireOp",EDGE,"E12.5.0.9"),sQuery(id+"F0.wireOp",EDGE,"E12.6.0.0"),sQuery(id+"F0.wireOp",EDGE,"E12.6.0.3"),sQuery(id+"F0.wireOp",EDGE,"E12.6.0.6"),sQuery(id+"F0.wireOp",EDGE,"E12.6.0.7"),sQuery(id+"F0.wireOp",EDGE,"E12.6.0.8"),sQuery(id+"F0.wireOp",EDGE,"E12.6.0.9"),sQuery(id+"F0.wireOp",EDGE,"E12.7.0.0"),sQuery(id+"F0.wireOp",EDGE,"E12.7.0.3"),sQuery(id+"F0.wireOp",EDGE,"E12.7.0.6"),sQuery(id+"F0.wireOp",EDGE,"E12.7.0.7"),sQuery(id+"F0.wireOp",EDGE,"E12.7.0.8"),sQuery(id+"F0.wireOp",EDGE,"E12.7.0.9"),sQuery(id+"F0.wireOp",EDGE,"E12.8.0.0"),sQuery(id+"F0.wireOp",EDGE,"E12.8.0.3"),sQuery(id+"F0.wireOp",EDGE,"E12.8.0.6"),sQuery(id+"F0.wireOp",EDGE,"E12.8.0.7"),sQuery(id+"F0.wireOp",EDGE,"E12.8.0.8"),sQuery(id+"F0.wireOp",EDGE,"E12.8.0.9"),sQuery(id+"F0.wireOp",EDGE,"E12.9.0.0"),sQuery(id+"F0.wireOp",EDGE,"E12.9.0.3"),sQuery(id+"F0.wireOp",EDGE,"E12.9.0.6"),sQuery(id+"F0.wireOp",EDGE,"E12.9.0.7"),sQuery(id+"F0.wireOp",EDGE,"E12.9.0.8"),sQuery(id+"F0.wireOp",EDGE,"E12.9.0.9"),sQuery(id+"F0.wireOp",EDGE,"E12.10.0.0"),sQuery(id+"F0.wireOp",EDGE,"E12.10.0.3"),sQuery(id+"F0.wireOp",EDGE,"E12.10.0.6"),sQuery(id+"F0.wireOp",EDGE,"E12.10.0.7"),sQuery(id+"F0.wireOp",EDGE,"E12.10.0.8"),sQuery(id+"F0.wireOp",EDGE,"E12.10.0.9"),sQuery(id+"F0.wireOp",EDGE,"E12.11.0.0"),sQuery(id+"F0.wireOp",EDGE,"E12.11.0.3"),sQuery(id+"F0.wireOp",EDGE,"E12.11.0.6"),sQuery(id+"F0.wireOp",EDGE,"E12.11.0.7"),sQuery(id+"F0.wireOp",EDGE,"E12.11.0.8"),sQuery(id+"F0.wireOp",EDGE,"E12.11.0.9"),sQuery(id+"F0.wireOp",EDGE,"E12.12.0.0"),sQuery(id+"F0.wireOp",EDGE,"E12.12.0.3"),sQuery(id+"F0.wireOp",EDGE,"E12.12.0.6"),sQuery(id+"F0.wireOp",EDGE,"E12.12.0.7"),sQuery(id+"F0.wireOp",EDGE,"E12.12.0.8"),sQuery(id+"F0.wireOp",EDGE,"E12.12.0.9"),sQuery(id+"F0.wireOp",EDGE,"E12.13.0.0"),sQuery(id+"F0.wireOp",EDGE,"E12.13.0.3"),sQuery(id+"F0.wireOp",EDGE,"E12.13.0.6"),sQuery(id+"F0.wireOp",EDGE,"E12.13.0.7"),sQuery(id+"F0.wireOp",EDGE,"E12.13.0.8"),sQuery(id+"F0.wireOp",EDGE,"E12.13.0.9"),sQuery(id+"F0.wireOp",EDGE,"E12.14.0.0"),sQuery(id+"F0.wireOp",EDGE,"E12.14.0.3"),sQuery(id+"F0.wireOp",EDGE,"E12.14.0.6"),sQuery(id+"F0.wireOp",EDGE,"E12.14.0.7"),sQuery(id+"F0.wireOp",EDGE,"E12.14.0.8"),sQuery(id+"F0.wireOp",EDGE,"E12.14.0.9"),sQuery(id+"F0.wireOp",EDGE,"E12.15.0.0"),sQuery(id+"F0.wireOp",EDGE,"E12.15.0.3"),sQuery(id+"F0.wireOp",EDGE,"E12.15.0.6"),sQuery(id+"F0.wireOp",EDGE,"E12.15.0.7"),sQuery(id+"F0.wireOp",EDGE,"E12.15.0.8"),sQuery(id+"F0.wireOp",EDGE,"E12.15.0.9"),sQuery(id+"F0.wireOp",EDGE,"E12.16.0.0"),sQuery(id+"F0.wireOp",EDGE,"E12.16.0.3"),sQuery(id+"F0.wireOp",EDGE,"E12.16.0.6"),sQuery(id+"F0.wireOp",EDGE,"E12.16.0.7"),sQuery(id+"F0.wireOp",EDGE,"E12.16.0.8"),sQuery(id+"F0.wireOp",EDGE,"E12.16.0.9"),sQuery(id+"F0.wireOp",EDGE,"E12.17.0.0"),sQuery(id+"F0.wireOp",EDGE,"E12.17.0.3"),sQuery(id+"F0.wireOp",EDGE,"E12.17.0.6"),sQuery(id+"F0.wireOp",EDGE,"E12.17.0.7"),sQuery(id+"F0.wireOp",EDGE,"E12.17.0.8"),sQuery(id+"F0.wireOp",EDGE,"E12.17.0.9"),sQuery(id+"F0.wireOp",EDGE,"E12.18.0.0"),sQuery(id+"F0.wireOp",EDGE,"E12.18.0.3"),sQuery(id+"F0.wireOp",EDGE,"E12.18.0.6"),sQuery(id+"F0.wireOp",EDGE,"E12.18.0.7"),sQuery(id+"F0.wireOp",EDGE,"E12.18.0.8"),sQuery(id+"F0.wireOp",EDGE,"E12.18.0.9"),sQuery(id+"F0.wireOp",EDGE,"E12.19.0.0"),sQuery(id+"F0.wireOp",EDGE,"E12.19.0.3"),sQuery(id+"F0.wireOp",EDGE,"E12.19.0.6"),sQuery(id+"F0.wireOp",EDGE,"E12.19.0.7"),sQuery(id+"F0.wireOp",EDGE,"E12.19.0.8"),sQuery(id+"F0.wireOp",EDGE,"E12.19.0.9"),sQuery(id+"F0.wireOp",EDGE,"E12.20.0.0"),sQuery(id+"F0.wireOp",EDGE,"E12.20.0.3"),sQuery(id+"F0.wireOp",EDGE,"E12.20.0.6"),sQuery(id+"F0.wireOp",EDGE,"E12.20.0.7"),sQuery(id+"F0.wireOp",EDGE,"E12.20.0.8"),sQuery(id+"F0.wireOp",EDGE,"E12.20.0.9")])]});
            hole(context, id + "F3", {"style" : HoleStyle.C_SINK, "endStyle" : HoleEndStyle.BLIND, "standardTappedOrClearance" : lookupTablePath({ "fit" : "Normal", "standard" : "ISO", "size" : "M3", "type" : "Clearance" }), "standardBlindInLast" : lookupTablePath({ "fit" : "Normal", "standard" : "ISO", "engagement" : "75%", "pitch" : "0.5 mm", "size" : "M3", "type" : "Clearance & tapped" }), "holeDiameter" : 3.4 * mm, "cSinkDiameter" : 6.72 * mm, "cSinkAngle" : 90 * degree, "majorDiameter" : 5 * mm, "holeDepth" : 22 * mm, "isTappedThrough" : true, "tappedDepth" : 20 * mm, "tapClearance" : 3, "locations" : qUnion([Q0, Q1, Q2]), "scope" : qUnion([Q3])});
        }
        {
            var Q0;
            Q0=makeQuery(id+"F1.opExtrude","SWEPT_EDGE",EDGE,{"disambiguationData":[OSD([sQuery(id+"F0.wireOp",EDGE,"E0.bottom"),sQuery(id+"F0.wireOp",EDGE,"E0.left")])]});
            var Q1;
            Q1=makeQuery(id+"F1.opExtrude","SWEPT_EDGE",EDGE,{"disambiguationData":[OSD([sQuery(id+"F0.wireOp",EDGE,"E0.top"),sQuery(id+"F0.wireOp",EDGE,"E0.left")])]});
            var Q2;
            Q2=makeQuery(id+"F1.opExtrude","SWEPT_EDGE",EDGE,{"disambiguationData":[OSD([sQuery(id+"F0.wireOp",EDGE,"E0.top"),sQuery(id+"F0.wireOp",EDGE,"E0.right")])]});
            var Q3;
            Q3=makeQuery(id+"F1.opExtrude","SWEPT_EDGE",EDGE,{"disambiguationData":[OSD([sQuery(id+"F0.wireOp",EDGE,"E0.bottom"),sQuery(id+"F0.wireOp",EDGE,"E0.right")])]});
            fillet(context, id + "F4", {"entities" : qUnion([Q0, Q1, Q2, Q3]), "radius" : 2 * mm, "tangentPropagation" : true});
        }
        {
            var Q0;
            Q0=makeQuery(id+"F1.opExtrude","CAP_FACE",FACE,{"disambiguationData":[OSD([sQuery(id+"F0.wireOp",EDGE,"E0.bottom"),sQuery(id+"F0.wireOp",EDGE,"E0.top"),sQuery(id+"F0.wireOp",EDGE,"E0.left"),sQuery(id+"F0.wireOp",EDGE,"E0.right"),sQuery(id+"F0.wireOp",EDGE,"E1.left"),sQuery(id+"F0.wireOp",EDGE,"E1.right"),sQuery(id+"F0.wireOp",EDGE,"E2.filletArc"),sQuery(id+"F0.wireOp",EDGE,"E3.filletArc"),sQuery(id+"F0.wireOp",EDGE,"E4.filletArc"),sQuery(id+"F0.wireOp",EDGE,"E5.filletArc"),sQuery(id+"F0.wireOp",EDGE,"E6.1.0.0"),sQuery(id+"F0.wireOp",EDGE,"E6.1.0.4"),sQuery(id+"F0.wireOp",EDGE,"E6.1.0.6"),sQuery(id+"F0.wireOp",EDGE,"E6.1.0.7"),sQuery(id+"F0.wireOp",EDGE,"E6.1.0.8"),sQuery(id+"F0.wireOp",EDGE,"E6.1.0.9"),sQuery(id+"F0.wireOp",EDGE,"E6.2.0.0"),sQuery(id+"F0.wireOp",EDGE,"E6.2.0.4"),sQuery(id+"F0.wireOp",EDGE,"E6.2.0.6"),sQuery(id+"F0.wireOp",EDGE,"E6.2.0.7"),sQuery(id+"F0.wireOp",EDGE,"E6.2.0.8"),sQuery(id+"F0.wireOp",EDGE,"E6.2.0.9"),sQuery(id+"F0.wireOp",EDGE,"E6.3.0.0"),sQuery(id+"F0.wireOp",EDGE,"E6.3.0.4"),sQuery(id+"F0.wireOp",EDGE,"E6.3.0.6"),sQuery(id+"F0.wireOp",EDGE,"E6.3.0.7"),sQuery(id+"F0.wireOp",EDGE,"E6.3.0.8"),sQuery(id+"F0.wireOp",EDGE,"E6.3.0.9"),sQuery(id+"F0.wireOp",EDGE,"E6.4.0.0"),sQuery(id+"F0.wireOp",EDGE,"E6.4.0.4"),sQuery(id+"F0.wireOp",EDGE,"E6.4.0.6"),sQuery(id+"F0.wireOp",EDGE,"E6.4.0.7"),sQuery(id+"F0.wireOp",EDGE,"E6.4.0.8"),sQuery(id+"F0.wireOp",EDGE,"E6.4.0.9"),sQuery(id+"F0.wireOp",EDGE,"E6.5.0.0"),sQuery(id+"F0.wireOp",EDGE,"E6.5.0.4"),sQuery(id+"F0.wireOp",EDGE,"E6.5.0.6"),sQuery(id+"F0.wireOp",EDGE,"E6.5.0.7"),sQuery(id+"F0.wireOp",EDGE,"E6.5.0.8"),sQuery(id+"F0.wireOp",EDGE,"E6.5.0.9"),sQuery(id+"F0.wireOp",EDGE,"E6.6.0.0"),sQuery(id+"F0.wireOp",EDGE,"E6.6.0.4"),sQuery(id+"F0.wireOp",EDGE,"E6.6.0.6"),sQuery(id+"F0.wireOp",EDGE,"E6.6.0.7"),sQuery(id+"F0.wireOp",EDGE,"E6.6.0.8"),sQuery(id+"F0.wireOp",EDGE,"E6.6.0.9"),sQuery(id+"F0.wireOp",EDGE,"E6.7.0.0"),sQuery(id+"F0.wireOp",EDGE,"E6.7.0.4"),sQuery(id+"F0.wireOp",EDGE,"E6.7.0.6"),sQuery(id+"F0.wireOp",EDGE,"E6.7.0.7"),sQuery(id+"F0.wireOp",EDGE,"E6.7.0.8"),sQuery(id+"F0.wireOp",EDGE,"E6.7.0.9"),sQuery(id+"F0.wireOp",EDGE,"E6.8.0.0"),sQuery(id+"F0.wireOp",EDGE,"E6.8.0.4"),sQuery(id+"F0.wireOp",EDGE,"E6.8.0.6"),sQuery(id+"F0.wireOp",EDGE,"E6.8.0.7"),sQuery(id+"F0.wireOp",EDGE,"E6.8.0.8"),sQuery(id+"F0.wireOp",EDGE,"E6.8.0.9"),sQuery(id+"F0.wireOp",EDGE,"E6.9.0.0"),sQuery(id+"F0.wireOp",EDGE,"E6.9.0.4"),sQuery(id+"F0.wireOp",EDGE,"E6.9.0.6"),sQuery(id+"F0.wireOp",EDGE,"E6.9.0.7"),sQuery(id+"F0.wireOp",EDGE,"E6.9.0.8"),sQuery(id+"F0.wireOp",EDGE,"E6.9.0.9"),sQuery(id+"F0.wireOp",EDGE,"E6.10.0.0"),sQuery(id+"F0.wireOp",EDGE,"E6.10.0.4"),sQuery(id+"F0.wireOp",EDGE,"E6.10.0.6"),sQuery(id+"F0.wireOp",EDGE,"E6.10.0.7"),sQuery(id+"F0.wireOp",EDGE,"E6.10.0.8"),sQuery(id+"F0.wireOp",EDGE,"E6.10.0.9"),sQuery(id+"F0.wireOp",EDGE,"E6.11.0.0"),sQuery(id+"F0.wireOp",EDGE,"E6.11.0.4"),sQuery(id+"F0.wireOp",EDGE,"E6.11.0.6"),sQuery(id+"F0.wireOp",EDGE,"E6.11.0.7"),sQuery(id+"F0.wireOp",EDGE,"E6.11.0.8"),sQuery(id+"F0.wireOp",EDGE,"E6.11.0.9"),sQuery(id+"F0.wireOp",EDGE,"E6.12.0.0"),sQuery(id+"F0.wireOp",EDGE,"E6.12.0.4"),sQuery(id+"F0.wireOp",EDGE,"E6.12.0.6"),sQuery(id+"F0.wireOp",EDGE,"E6.12.0.7"),sQuery(id+"F0.wireOp",EDGE,"E6.12.0.8"),sQuery(id+"F0.wireOp",EDGE,"E6.12.0.9"),sQuery(id+"F0.wireOp",EDGE,"E6.13.0.0"),sQuery(id+"F0.wireOp",EDGE,"E6.13.0.4"),sQuery(id+"F0.wireOp",EDGE,"E6.13.0.6"),sQuery(id+"F0.wireOp",EDGE,"E6.13.0.7"),sQuery(id+"F0.wireOp",EDGE,"E6.13.0.8"),sQuery(id+"F0.wireOp",EDGE,"E6.13.0.9"),sQuery(id+"F0.wireOp",EDGE,"E6.14.0.0"),sQuery(id+"F0.wireOp",EDGE,"E6.14.0.4"),sQuery(id+"F0.wireOp",EDGE,"E6.14.0.6"),sQuery(id+"F0.wireOp",EDGE,"E6.14.0.7"),sQuery(id+"F0.wireOp",EDGE,"E6.14.0.8"),sQuery(id+"F0.wireOp",EDGE,"E6.14.0.9"),sQuery(id+"F0.wireOp",EDGE,"E6.15.0.0"),sQuery(id+"F0.wireOp",EDGE,"E6.15.0.4"),sQuery(id+"F0.wireOp",EDGE,"E6.15.0.6"),sQuery(id+"F0.wireOp",EDGE,"E6.15.0.7"),sQuery(id+"F0.wireOp",EDGE,"E6.15.0.8"),sQuery(id+"F0.wireOp",EDGE,"E6.15.0.9"),sQuery(id+"F0.wireOp",EDGE,"E6.16.0.0"),sQuery(id+"F0.wireOp",EDGE,"E6.16.0.4"),sQuery(id+"F0.wireOp",EDGE,"E6.16.0.6"),sQuery(id+"F0.wireOp",EDGE,"E6.16.0.7"),sQuery(id+"F0.wireOp",EDGE,"E6.16.0.8"),sQuery(id+"F0.wireOp",EDGE,"E6.16.0.9"),sQuery(id+"F0.wireOp",EDGE,"E6.17.0.0"),sQuery(id+"F0.wireOp",EDGE,"E6.17.0.4"),sQuery(id+"F0.wireOp",EDGE,"E6.17.0.6"),sQuery(id+"F0.wireOp",EDGE,"E6.17.0.7"),sQuery(id+"F0.wireOp",EDGE,"E6.17.0.8"),sQuery(id+"F0.wireOp",EDGE,"E6.17.0.9"),sQuery(id+"F0.wireOp",EDGE,"E6.18.0.0"),sQuery(id+"F0.wireOp",EDGE,"E6.18.0.4"),sQuery(id+"F0.wireOp",EDGE,"E6.18.0.6"),sQuery(id+"F0.wireOp",EDGE,"E6.18.0.7"),sQuery(id+"F0.wireOp",EDGE,"E6.18.0.8"),sQuery(id+"F0.wireOp",EDGE,"E6.18.0.9"),sQuery(id+"F0.wireOp",EDGE,"E6.19.0.0"),sQuery(id+"F0.wireOp",EDGE,"E6.19.0.4"),sQuery(id+"F0.wireOp",EDGE,"E6.19.0.6"),sQuery(id+"F0.wireOp",EDGE,"E6.19.0.7"),sQuery(id+"F0.wireOp",EDGE,"E6.19.0.8"),sQuery(id+"F0.wireOp",EDGE,"E6.19.0.9"),sQuery(id+"F0.wireOp",EDGE,"E6.20.0.0"),sQuery(id+"F0.wireOp",EDGE,"E6.20.0.4"),sQuery(id+"F0.wireOp",EDGE,"E6.20.0.6"),sQuery(id+"F0.wireOp",EDGE,"E6.20.0.7"),sQuery(id+"F0.wireOp",EDGE,"E6.20.0.8"),sQuery(id+"F0.wireOp",EDGE,"E6.20.0.9"),sQuery(id+"F0.wireOp",EDGE,"E7.left"),sQuery(id+"F0.wireOp",EDGE,"E7.right"),sQuery(id+"F0.wireOp",EDGE,"E8.filletArc"),sQuery(id+"F0.wireOp",EDGE,"E9.filletArc"),sQuery(id+"F0.wireOp",EDGE,"E10.filletArc"),sQuery(id+"F0.wireOp",EDGE,"E11.filletArc"),sQuery(id+"F0.wireOp",EDGE,"E12.1.0.0"),sQuery(id+"F0.wireOp",EDGE,"E12.1.0.3"),sQuery(id+"F0.wireOp",EDGE,"E12.1.0.6"),sQuery(id+"F0.wireOp",EDGE,"E12.1.0.7"),sQuery(id+"F0.wireOp",EDGE,"E12.1.0.8"),sQuery(id+"F0.wireOp",EDGE,"E12.1.0.9"),sQuery(id+"F0.wireOp",EDGE,"E12.2.0.0"),sQuery(id+"F0.wireOp",EDGE,"E12.2.0.3"),sQuery(id+"F0.wireOp",EDGE,"E12.2.0.6"),sQuery(id+"F0.wireOp",EDGE,"E12.2.0.7"),sQuery(id+"F0.wireOp",EDGE,"E12.2.0.8"),sQuery(id+"F0.wireOp",EDGE,"E12.2.0.9"),sQuery(id+"F0.wireOp",EDGE,"E12.3.0.0"),sQuery(id+"F0.wireOp",EDGE,"E12.3.0.3"),sQuery(id+"F0.wireOp",EDGE,"E12.3.0.6"),sQuery(id+"F0.wireOp",EDGE,"E12.3.0.7"),sQuery(id+"F0.wireOp",EDGE,"E12.3.0.8"),sQuery(id+"F0.wireOp",EDGE,"E12.3.0.9"),sQuery(id+"F0.wireOp",EDGE,"E12.4.0.0"),sQuery(id+"F0.wireOp",EDGE,"E12.4.0.3"),sQuery(id+"F0.wireOp",EDGE,"E12.4.0.6"),sQuery(id+"F0.wireOp",EDGE,"E12.4.0.7"),sQuery(id+"F0.wireOp",EDGE,"E12.4.0.8"),sQuery(id+"F0.wireOp",EDGE,"E12.4.0.9"),sQuery(id+"F0.wireOp",EDGE,"E12.5.0.0"),sQuery(id+"F0.wireOp",EDGE,"E12.5.0.3"),sQuery(id+"F0.wireOp",EDGE,"E12.5.0.6"),sQuery(id+"F0.wireOp",EDGE,"E12.5.0.7"),sQuery(id+"F0.wireOp",EDGE,"E12.5.0.8"),sQuery(id+"F0.wireOp",EDGE,"E12.5.0.9"),sQuery(id+"F0.wireOp",EDGE,"E12.6.0.0"),sQuery(id+"F0.wireOp",EDGE,"E12.6.0.3"),sQuery(id+"F0.wireOp",EDGE,"E12.6.0.6"),sQuery(id+"F0.wireOp",EDGE,"E12.6.0.7"),sQuery(id+"F0.wireOp",EDGE,"E12.6.0.8"),sQuery(id+"F0.wireOp",EDGE,"E12.6.0.9"),sQuery(id+"F0.wireOp",EDGE,"E12.7.0.0"),sQuery(id+"F0.wireOp",EDGE,"E12.7.0.3"),sQuery(id+"F0.wireOp",EDGE,"E12.7.0.6"),sQuery(id+"F0.wireOp",EDGE,"E12.7.0.7"),sQuery(id+"F0.wireOp",EDGE,"E12.7.0.8"),sQuery(id+"F0.wireOp",EDGE,"E12.7.0.9"),sQuery(id+"F0.wireOp",EDGE,"E12.8.0.0"),sQuery(id+"F0.wireOp",EDGE,"E12.8.0.3"),sQuery(id+"F0.wireOp",EDGE,"E12.8.0.6"),sQuery(id+"F0.wireOp",EDGE,"E12.8.0.7"),sQuery(id+"F0.wireOp",EDGE,"E12.8.0.8"),sQuery(id+"F0.wireOp",EDGE,"E12.8.0.9"),sQuery(id+"F0.wireOp",EDGE,"E12.9.0.0"),sQuery(id+"F0.wireOp",EDGE,"E12.9.0.3"),sQuery(id+"F0.wireOp",EDGE,"E12.9.0.6"),sQuery(id+"F0.wireOp",EDGE,"E12.9.0.7"),sQuery(id+"F0.wireOp",EDGE,"E12.9.0.8"),sQuery(id+"F0.wireOp",EDGE,"E12.9.0.9"),sQuery(id+"F0.wireOp",EDGE,"E12.10.0.0"),sQuery(id+"F0.wireOp",EDGE,"E12.10.0.3"),sQuery(id+"F0.wireOp",EDGE,"E12.10.0.6"),sQuery(id+"F0.wireOp",EDGE,"E12.10.0.7"),sQuery(id+"F0.wireOp",EDGE,"E12.10.0.8"),sQuery(id+"F0.wireOp",EDGE,"E12.10.0.9"),sQuery(id+"F0.wireOp",EDGE,"E12.11.0.0"),sQuery(id+"F0.wireOp",EDGE,"E12.11.0.3"),sQuery(id+"F0.wireOp",EDGE,"E12.11.0.6"),sQuery(id+"F0.wireOp",EDGE,"E12.11.0.7"),sQuery(id+"F0.wireOp",EDGE,"E12.11.0.8"),sQuery(id+"F0.wireOp",EDGE,"E12.11.0.9"),sQuery(id+"F0.wireOp",EDGE,"E12.12.0.0"),sQuery(id+"F0.wireOp",EDGE,"E12.12.0.3"),sQuery(id+"F0.wireOp",EDGE,"E12.12.0.6"),sQuery(id+"F0.wireOp",EDGE,"E12.12.0.7"),sQuery(id+"F0.wireOp",EDGE,"E12.12.0.8"),sQuery(id+"F0.wireOp",EDGE,"E12.12.0.9"),sQuery(id+"F0.wireOp",EDGE,"E12.13.0.0"),sQuery(id+"F0.wireOp",EDGE,"E12.13.0.3"),sQuery(id+"F0.wireOp",EDGE,"E12.13.0.6"),sQuery(id+"F0.wireOp",EDGE,"E12.13.0.7"),sQuery(id+"F0.wireOp",EDGE,"E12.13.0.8"),sQuery(id+"F0.wireOp",EDGE,"E12.13.0.9"),sQuery(id+"F0.wireOp",EDGE,"E12.14.0.0"),sQuery(id+"F0.wireOp",EDGE,"E12.14.0.3"),sQuery(id+"F0.wireOp",EDGE,"E12.14.0.6"),sQuery(id+"F0.wireOp",EDGE,"E12.14.0.7"),sQuery(id+"F0.wireOp",EDGE,"E12.14.0.8"),sQuery(id+"F0.wireOp",EDGE,"E12.14.0.9"),sQuery(id+"F0.wireOp",EDGE,"E12.15.0.0"),sQuery(id+"F0.wireOp",EDGE,"E12.15.0.3"),sQuery(id+"F0.wireOp",EDGE,"E12.15.0.6"),sQuery(id+"F0.wireOp",EDGE,"E12.15.0.7"),sQuery(id+"F0.wireOp",EDGE,"E12.15.0.8"),sQuery(id+"F0.wireOp",EDGE,"E12.15.0.9"),sQuery(id+"F0.wireOp",EDGE,"E12.16.0.0"),sQuery(id+"F0.wireOp",EDGE,"E12.16.0.3"),sQuery(id+"F0.wireOp",EDGE,"E12.16.0.6"),sQuery(id+"F0.wireOp",EDGE,"E12.16.0.7"),sQuery(id+"F0.wireOp",EDGE,"E12.16.0.8"),sQuery(id+"F0.wireOp",EDGE,"E12.16.0.9"),sQuery(id+"F0.wireOp",EDGE,"E12.17.0.0"),sQuery(id+"F0.wireOp",EDGE,"E12.17.0.3"),sQuery(id+"F0.wireOp",EDGE,"E12.17.0.6"),sQuery(id+"F0.wireOp",EDGE,"E12.17.0.7"),sQuery(id+"F0.wireOp",EDGE,"E12.17.0.8"),sQuery(id+"F0.wireOp",EDGE,"E12.17.0.9"),sQuery(id+"F0.wireOp",EDGE,"E12.18.0.0"),sQuery(id+"F0.wireOp",EDGE,"E12.18.0.3"),sQuery(id+"F0.wireOp",EDGE,"E12.18.0.6"),sQuery(id+"F0.wireOp",EDGE,"E12.18.0.7"),sQuery(id+"F0.wireOp",EDGE,"E12.18.0.8"),sQuery(id+"F0.wireOp",EDGE,"E12.18.0.9"),sQuery(id+"F0.wireOp",EDGE,"E12.19.0.0"),sQuery(id+"F0.wireOp",EDGE,"E12.19.0.3"),sQuery(id+"F0.wireOp",EDGE,"E12.19.0.6"),sQuery(id+"F0.wireOp",EDGE,"E12.19.0.7"),sQuery(id+"F0.wireOp",EDGE,"E12.19.0.8"),sQuery(id+"F0.wireOp",EDGE,"E12.19.0.9"),sQuery(id+"F0.wireOp",EDGE,"E12.20.0.0"),sQuery(id+"F0.wireOp",EDGE,"E12.20.0.3"),sQuery(id+"F0.wireOp",EDGE,"E12.20.0.6"),sQuery(id+"F0.wireOp",EDGE,"E12.20.0.7"),sQuery(id+"F0.wireOp",EDGE,"E12.20.0.8"),sQuery(id+"F0.wireOp",EDGE,"E12.20.0.9")])],"isStart":true});
            var Q1;
            Q1=makeQuery(id+"F1.opExtrude","CAP_FACE",FACE,{"disambiguationData":[OSD([sQuery(id+"F0.wireOp",EDGE,"E0.bottom"),sQuery(id+"F0.wireOp",EDGE,"E0.top"),sQuery(id+"F0.wireOp",EDGE,"E0.left"),sQuery(id+"F0.wireOp",EDGE,"E0.right"),sQuery(id+"F0.wireOp",EDGE,"E1.left"),sQuery(id+"F0.wireOp",EDGE,"E1.right"),sQuery(id+"F0.wireOp",EDGE,"E2.filletArc"),sQuery(id+"F0.wireOp",EDGE,"E3.filletArc"),sQuery(id+"F0.wireOp",EDGE,"E4.filletArc"),sQuery(id+"F0.wireOp",EDGE,"E5.filletArc"),sQuery(id+"F0.wireOp",EDGE,"E6.1.0.0"),sQuery(id+"F0.wireOp",EDGE,"E6.1.0.4"),sQuery(id+"F0.wireOp",EDGE,"E6.1.0.6"),sQuery(id+"F0.wireOp",EDGE,"E6.1.0.7"),sQuery(id+"F0.wireOp",EDGE,"E6.1.0.8"),sQuery(id+"F0.wireOp",EDGE,"E6.1.0.9"),sQuery(id+"F0.wireOp",EDGE,"E6.2.0.0"),sQuery(id+"F0.wireOp",EDGE,"E6.2.0.4"),sQuery(id+"F0.wireOp",EDGE,"E6.2.0.6"),sQuery(id+"F0.wireOp",EDGE,"E6.2.0.7"),sQuery(id+"F0.wireOp",EDGE,"E6.2.0.8"),sQuery(id+"F0.wireOp",EDGE,"E6.2.0.9"),sQuery(id+"F0.wireOp",EDGE,"E6.3.0.0"),sQuery(id+"F0.wireOp",EDGE,"E6.3.0.4"),sQuery(id+"F0.wireOp",EDGE,"E6.3.0.6"),sQuery(id+"F0.wireOp",EDGE,"E6.3.0.7"),sQuery(id+"F0.wireOp",EDGE,"E6.3.0.8"),sQuery(id+"F0.wireOp",EDGE,"E6.3.0.9"),sQuery(id+"F0.wireOp",EDGE,"E6.4.0.0"),sQuery(id+"F0.wireOp",EDGE,"E6.4.0.4"),sQuery(id+"F0.wireOp",EDGE,"E6.4.0.6"),sQuery(id+"F0.wireOp",EDGE,"E6.4.0.7"),sQuery(id+"F0.wireOp",EDGE,"E6.4.0.8"),sQuery(id+"F0.wireOp",EDGE,"E6.4.0.9"),sQuery(id+"F0.wireOp",EDGE,"E6.5.0.0"),sQuery(id+"F0.wireOp",EDGE,"E6.5.0.4"),sQuery(id+"F0.wireOp",EDGE,"E6.5.0.6"),sQuery(id+"F0.wireOp",EDGE,"E6.5.0.7"),sQuery(id+"F0.wireOp",EDGE,"E6.5.0.8"),sQuery(id+"F0.wireOp",EDGE,"E6.5.0.9"),sQuery(id+"F0.wireOp",EDGE,"E6.6.0.0"),sQuery(id+"F0.wireOp",EDGE,"E6.6.0.4"),sQuery(id+"F0.wireOp",EDGE,"E6.6.0.6"),sQuery(id+"F0.wireOp",EDGE,"E6.6.0.7"),sQuery(id+"F0.wireOp",EDGE,"E6.6.0.8"),sQuery(id+"F0.wireOp",EDGE,"E6.6.0.9"),sQuery(id+"F0.wireOp",EDGE,"E6.7.0.0"),sQuery(id+"F0.wireOp",EDGE,"E6.7.0.4"),sQuery(id+"F0.wireOp",EDGE,"E6.7.0.6"),sQuery(id+"F0.wireOp",EDGE,"E6.7.0.7"),sQuery(id+"F0.wireOp",EDGE,"E6.7.0.8"),sQuery(id+"F0.wireOp",EDGE,"E6.7.0.9"),sQuery(id+"F0.wireOp",EDGE,"E6.8.0.0"),sQuery(id+"F0.wireOp",EDGE,"E6.8.0.4"),sQuery(id+"F0.wireOp",EDGE,"E6.8.0.6"),sQuery(id+"F0.wireOp",EDGE,"E6.8.0.7"),sQuery(id+"F0.wireOp",EDGE,"E6.8.0.8"),sQuery(id+"F0.wireOp",EDGE,"E6.8.0.9"),sQuery(id+"F0.wireOp",EDGE,"E6.9.0.0"),sQuery(id+"F0.wireOp",EDGE,"E6.9.0.4"),sQuery(id+"F0.wireOp",EDGE,"E6.9.0.6"),sQuery(id+"F0.wireOp",EDGE,"E6.9.0.7"),sQuery(id+"F0.wireOp",EDGE,"E6.9.0.8"),sQuery(id+"F0.wireOp",EDGE,"E6.9.0.9"),sQuery(id+"F0.wireOp",EDGE,"E6.10.0.0"),sQuery(id+"F0.wireOp",EDGE,"E6.10.0.4"),sQuery(id+"F0.wireOp",EDGE,"E6.10.0.6"),sQuery(id+"F0.wireOp",EDGE,"E6.10.0.7"),sQuery(id+"F0.wireOp",EDGE,"E6.10.0.8"),sQuery(id+"F0.wireOp",EDGE,"E6.10.0.9"),sQuery(id+"F0.wireOp",EDGE,"E6.11.0.0"),sQuery(id+"F0.wireOp",EDGE,"E6.11.0.4"),sQuery(id+"F0.wireOp",EDGE,"E6.11.0.6"),sQuery(id+"F0.wireOp",EDGE,"E6.11.0.7"),sQuery(id+"F0.wireOp",EDGE,"E6.11.0.8"),sQuery(id+"F0.wireOp",EDGE,"E6.11.0.9"),sQuery(id+"F0.wireOp",EDGE,"E6.12.0.0"),sQuery(id+"F0.wireOp",EDGE,"E6.12.0.4"),sQuery(id+"F0.wireOp",EDGE,"E6.12.0.6"),sQuery(id+"F0.wireOp",EDGE,"E6.12.0.7"),sQuery(id+"F0.wireOp",EDGE,"E6.12.0.8"),sQuery(id+"F0.wireOp",EDGE,"E6.12.0.9"),sQuery(id+"F0.wireOp",EDGE,"E6.13.0.0"),sQuery(id+"F0.wireOp",EDGE,"E6.13.0.4"),sQuery(id+"F0.wireOp",EDGE,"E6.13.0.6"),sQuery(id+"F0.wireOp",EDGE,"E6.13.0.7"),sQuery(id+"F0.wireOp",EDGE,"E6.13.0.8"),sQuery(id+"F0.wireOp",EDGE,"E6.13.0.9"),sQuery(id+"F0.wireOp",EDGE,"E6.14.0.0"),sQuery(id+"F0.wireOp",EDGE,"E6.14.0.4"),sQuery(id+"F0.wireOp",EDGE,"E6.14.0.6"),sQuery(id+"F0.wireOp",EDGE,"E6.14.0.7"),sQuery(id+"F0.wireOp",EDGE,"E6.14.0.8"),sQuery(id+"F0.wireOp",EDGE,"E6.14.0.9"),sQuery(id+"F0.wireOp",EDGE,"E6.15.0.0"),sQuery(id+"F0.wireOp",EDGE,"E6.15.0.4"),sQuery(id+"F0.wireOp",EDGE,"E6.15.0.6"),sQuery(id+"F0.wireOp",EDGE,"E6.15.0.7"),sQuery(id+"F0.wireOp",EDGE,"E6.15.0.8"),sQuery(id+"F0.wireOp",EDGE,"E6.15.0.9"),sQuery(id+"F0.wireOp",EDGE,"E6.16.0.0"),sQuery(id+"F0.wireOp",EDGE,"E6.16.0.4"),sQuery(id+"F0.wireOp",EDGE,"E6.16.0.6"),sQuery(id+"F0.wireOp",EDGE,"E6.16.0.7"),sQuery(id+"F0.wireOp",EDGE,"E6.16.0.8"),sQuery(id+"F0.wireOp",EDGE,"E6.16.0.9"),sQuery(id+"F0.wireOp",EDGE,"E6.17.0.0"),sQuery(id+"F0.wireOp",EDGE,"E6.17.0.4"),sQuery(id+"F0.wireOp",EDGE,"E6.17.0.6"),sQuery(id+"F0.wireOp",EDGE,"E6.17.0.7"),sQuery(id+"F0.wireOp",EDGE,"E6.17.0.8"),sQuery(id+"F0.wireOp",EDGE,"E6.17.0.9"),sQuery(id+"F0.wireOp",EDGE,"E6.18.0.0"),sQuery(id+"F0.wireOp",EDGE,"E6.18.0.4"),sQuery(id+"F0.wireOp",EDGE,"E6.18.0.6"),sQuery(id+"F0.wireOp",EDGE,"E6.18.0.7"),sQuery(id+"F0.wireOp",EDGE,"E6.18.0.8"),sQuery(id+"F0.wireOp",EDGE,"E6.18.0.9"),sQuery(id+"F0.wireOp",EDGE,"E6.19.0.0"),sQuery(id+"F0.wireOp",EDGE,"E6.19.0.4"),sQuery(id+"F0.wireOp",EDGE,"E6.19.0.6"),sQuery(id+"F0.wireOp",EDGE,"E6.19.0.7"),sQuery(id+"F0.wireOp",EDGE,"E6.19.0.8"),sQuery(id+"F0.wireOp",EDGE,"E6.19.0.9"),sQuery(id+"F0.wireOp",EDGE,"E6.20.0.0"),sQuery(id+"F0.wireOp",EDGE,"E6.20.0.4"),sQuery(id+"F0.wireOp",EDGE,"E6.20.0.6"),sQuery(id+"F0.wireOp",EDGE,"E6.20.0.7"),sQuery(id+"F0.wireOp",EDGE,"E6.20.0.8"),sQuery(id+"F0.wireOp",EDGE,"E6.20.0.9"),sQuery(id+"F0.wireOp",EDGE,"E7.left"),sQuery(id+"F0.wireOp",EDGE,"E7.right"),sQuery(id+"F0.wireOp",EDGE,"E8.filletArc"),sQuery(id+"F0.wireOp",EDGE,"E9.filletArc"),sQuery(id+"F0.wireOp",EDGE,"E10.filletArc"),sQuery(id+"F0.wireOp",EDGE,"E11.filletArc"),sQuery(id+"F0.wireOp",EDGE,"E12.1.0.0"),sQuery(id+"F0.wireOp",EDGE,"E12.1.0.3"),sQuery(id+"F0.wireOp",EDGE,"E12.1.0.6"),sQuery(id+"F0.wireOp",EDGE,"E12.1.0.7"),sQuery(id+"F0.wireOp",EDGE,"E12.1.0.8"),sQuery(id+"F0.wireOp",EDGE,"E12.1.0.9"),sQuery(id+"F0.wireOp",EDGE,"E12.2.0.0"),sQuery(id+"F0.wireOp",EDGE,"E12.2.0.3"),sQuery(id+"F0.wireOp",EDGE,"E12.2.0.6"),sQuery(id+"F0.wireOp",EDGE,"E12.2.0.7"),sQuery(id+"F0.wireOp",EDGE,"E12.2.0.8"),sQuery(id+"F0.wireOp",EDGE,"E12.2.0.9"),sQuery(id+"F0.wireOp",EDGE,"E12.3.0.0"),sQuery(id+"F0.wireOp",EDGE,"E12.3.0.3"),sQuery(id+"F0.wireOp",EDGE,"E12.3.0.6"),sQuery(id+"F0.wireOp",EDGE,"E12.3.0.7"),sQuery(id+"F0.wireOp",EDGE,"E12.3.0.8"),sQuery(id+"F0.wireOp",EDGE,"E12.3.0.9"),sQuery(id+"F0.wireOp",EDGE,"E12.4.0.0"),sQuery(id+"F0.wireOp",EDGE,"E12.4.0.3"),sQuery(id+"F0.wireOp",EDGE,"E12.4.0.6"),sQuery(id+"F0.wireOp",EDGE,"E12.4.0.7"),sQuery(id+"F0.wireOp",EDGE,"E12.4.0.8"),sQuery(id+"F0.wireOp",EDGE,"E12.4.0.9"),sQuery(id+"F0.wireOp",EDGE,"E12.5.0.0"),sQuery(id+"F0.wireOp",EDGE,"E12.5.0.3"),sQuery(id+"F0.wireOp",EDGE,"E12.5.0.6"),sQuery(id+"F0.wireOp",EDGE,"E12.5.0.7"),sQuery(id+"F0.wireOp",EDGE,"E12.5.0.8"),sQuery(id+"F0.wireOp",EDGE,"E12.5.0.9"),sQuery(id+"F0.wireOp",EDGE,"E12.6.0.0"),sQuery(id+"F0.wireOp",EDGE,"E12.6.0.3"),sQuery(id+"F0.wireOp",EDGE,"E12.6.0.6"),sQuery(id+"F0.wireOp",EDGE,"E12.6.0.7"),sQuery(id+"F0.wireOp",EDGE,"E12.6.0.8"),sQuery(id+"F0.wireOp",EDGE,"E12.6.0.9"),sQuery(id+"F0.wireOp",EDGE,"E12.7.0.0"),sQuery(id+"F0.wireOp",EDGE,"E12.7.0.3"),sQuery(id+"F0.wireOp",EDGE,"E12.7.0.6"),sQuery(id+"F0.wireOp",EDGE,"E12.7.0.7"),sQuery(id+"F0.wireOp",EDGE,"E12.7.0.8"),sQuery(id+"F0.wireOp",EDGE,"E12.7.0.9"),sQuery(id+"F0.wireOp",EDGE,"E12.8.0.0"),sQuery(id+"F0.wireOp",EDGE,"E12.8.0.3"),sQuery(id+"F0.wireOp",EDGE,"E12.8.0.6"),sQuery(id+"F0.wireOp",EDGE,"E12.8.0.7"),sQuery(id+"F0.wireOp",EDGE,"E12.8.0.8"),sQuery(id+"F0.wireOp",EDGE,"E12.8.0.9"),sQuery(id+"F0.wireOp",EDGE,"E12.9.0.0"),sQuery(id+"F0.wireOp",EDGE,"E12.9.0.3"),sQuery(id+"F0.wireOp",EDGE,"E12.9.0.6"),sQuery(id+"F0.wireOp",EDGE,"E12.9.0.7"),sQuery(id+"F0.wireOp",EDGE,"E12.9.0.8"),sQuery(id+"F0.wireOp",EDGE,"E12.9.0.9"),sQuery(id+"F0.wireOp",EDGE,"E12.10.0.0"),sQuery(id+"F0.wireOp",EDGE,"E12.10.0.3"),sQuery(id+"F0.wireOp",EDGE,"E12.10.0.6"),sQuery(id+"F0.wireOp",EDGE,"E12.10.0.7"),sQuery(id+"F0.wireOp",EDGE,"E12.10.0.8"),sQuery(id+"F0.wireOp",EDGE,"E12.10.0.9"),sQuery(id+"F0.wireOp",EDGE,"E12.11.0.0"),sQuery(id+"F0.wireOp",EDGE,"E12.11.0.3"),sQuery(id+"F0.wireOp",EDGE,"E12.11.0.6"),sQuery(id+"F0.wireOp",EDGE,"E12.11.0.7"),sQuery(id+"F0.wireOp",EDGE,"E12.11.0.8"),sQuery(id+"F0.wireOp",EDGE,"E12.11.0.9"),sQuery(id+"F0.wireOp",EDGE,"E12.12.0.0"),sQuery(id+"F0.wireOp",EDGE,"E12.12.0.3"),sQuery(id+"F0.wireOp",EDGE,"E12.12.0.6"),sQuery(id+"F0.wireOp",EDGE,"E12.12.0.7"),sQuery(id+"F0.wireOp",EDGE,"E12.12.0.8"),sQuery(id+"F0.wireOp",EDGE,"E12.12.0.9"),sQuery(id+"F0.wireOp",EDGE,"E12.13.0.0"),sQuery(id+"F0.wireOp",EDGE,"E12.13.0.3"),sQuery(id+"F0.wireOp",EDGE,"E12.13.0.6"),sQuery(id+"F0.wireOp",EDGE,"E12.13.0.7"),sQuery(id+"F0.wireOp",EDGE,"E12.13.0.8"),sQuery(id+"F0.wireOp",EDGE,"E12.13.0.9"),sQuery(id+"F0.wireOp",EDGE,"E12.14.0.0"),sQuery(id+"F0.wireOp",EDGE,"E12.14.0.3"),sQuery(id+"F0.wireOp",EDGE,"E12.14.0.6"),sQuery(id+"F0.wireOp",EDGE,"E12.14.0.7"),sQuery(id+"F0.wireOp",EDGE,"E12.14.0.8"),sQuery(id+"F0.wireOp",EDGE,"E12.14.0.9"),sQuery(id+"F0.wireOp",EDGE,"E12.15.0.0"),sQuery(id+"F0.wireOp",EDGE,"E12.15.0.3"),sQuery(id+"F0.wireOp",EDGE,"E12.15.0.6"),sQuery(id+"F0.wireOp",EDGE,"E12.15.0.7"),sQuery(id+"F0.wireOp",EDGE,"E12.15.0.8"),sQuery(id+"F0.wireOp",EDGE,"E12.15.0.9"),sQuery(id+"F0.wireOp",EDGE,"E12.16.0.0"),sQuery(id+"F0.wireOp",EDGE,"E12.16.0.3"),sQuery(id+"F0.wireOp",EDGE,"E12.16.0.6"),sQuery(id+"F0.wireOp",EDGE,"E12.16.0.7"),sQuery(id+"F0.wireOp",EDGE,"E12.16.0.8"),sQuery(id+"F0.wireOp",EDGE,"E12.16.0.9"),sQuery(id+"F0.wireOp",EDGE,"E12.17.0.0"),sQuery(id+"F0.wireOp",EDGE,"E12.17.0.3"),sQuery(id+"F0.wireOp",EDGE,"E12.17.0.6"),sQuery(id+"F0.wireOp",EDGE,"E12.17.0.7"),sQuery(id+"F0.wireOp",EDGE,"E12.17.0.8"),sQuery(id+"F0.wireOp",EDGE,"E12.17.0.9"),sQuery(id+"F0.wireOp",EDGE,"E12.18.0.0"),sQuery(id+"F0.wireOp",EDGE,"E12.18.0.3"),sQuery(id+"F0.wireOp",EDGE,"E12.18.0.6"),sQuery(id+"F0.wireOp",EDGE,"E12.18.0.7"),sQuery(id+"F0.wireOp",EDGE,"E12.18.0.8"),sQuery(id+"F0.wireOp",EDGE,"E12.18.0.9"),sQuery(id+"F0.wireOp",EDGE,"E12.19.0.0"),sQuery(id+"F0.wireOp",EDGE,"E12.19.0.3"),sQuery(id+"F0.wireOp",EDGE,"E12.19.0.6"),sQuery(id+"F0.wireOp",EDGE,"E12.19.0.7"),sQuery(id+"F0.wireOp",EDGE,"E12.19.0.8"),sQuery(id+"F0.wireOp",EDGE,"E12.19.0.9"),sQuery(id+"F0.wireOp",EDGE,"E12.20.0.0"),sQuery(id+"F0.wireOp",EDGE,"E12.20.0.3"),sQuery(id+"F0.wireOp",EDGE,"E12.20.0.6"),sQuery(id+"F0.wireOp",EDGE,"E12.20.0.7"),sQuery(id+"F0.wireOp",EDGE,"E12.20.0.8"),sQuery(id+"F0.wireOp",EDGE,"E12.20.0.9")])],"isStart":false});
            chamfer(context, id + "F5", {"entities" : qUnion([Q0, Q1]), "width" : .4 * mm, "tangentPropagation" : true});
        }
    });
